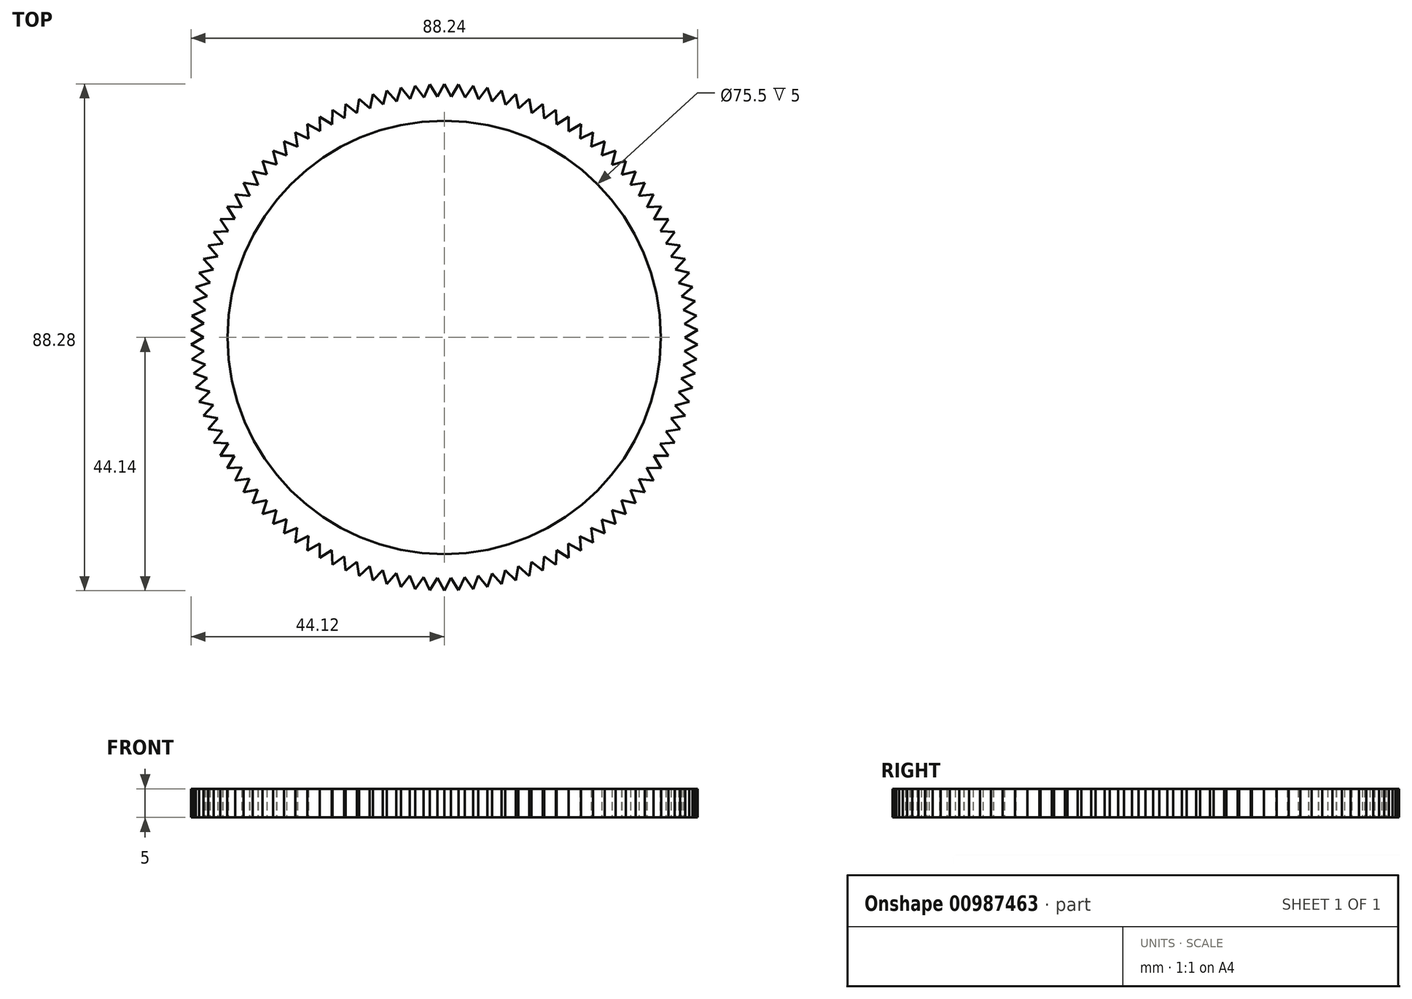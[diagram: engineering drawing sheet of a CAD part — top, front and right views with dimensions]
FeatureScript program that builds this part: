
annotation { "Feature Type Name" : "Feature", "Feature Type Description" : "" }
export const myFeature = defineFeature(function(context is Context, id is Id, definition is map)
    precondition{}
    {
        {
            var Q0;
            Q0=qCreatedBy(makeId("Top.planeOp"),FACE);
            var sketch = newSketch(context, id + "F0", { "sketchPlane" : qUnion([Q0])});
            skCircle(sketch, "E0", {"center": v(0, 0) * mm, "radius": 37.75 * mm});
            skCircle(sketch, "E1", {"center": v(0, 0) * mm, "radius": 41.84 * mm});
            skLineSegment(sketch, "E2", {"start": v(-1.23, 41.82) * mm, "end": v(0, 44.14) * mm});
            skLineSegment(sketch, "E3", {"start": v(0, 44.14) * mm, "end": v(1.27, 41.82) * mm});
            skLineSegment(sketch, "E4.1.0", {"start": v(-3.61, 41.69) * mm, "end": v(-2.52, 44.07) * mm});
            skLineSegment(sketch, "E4.1.1", {"start": v(-2.52, 44.07) * mm, "end": v(-1.12, 41.83) * mm});
            skLineSegment(sketch, "E4.2.0", {"start": v(-5.99, 41.41) * mm, "end": v(-5.03, 43.85) * mm});
            skLineSegment(sketch, "E4.2.1", {"start": v(-5.03, 43.85) * mm, "end": v(-3.5, 41.7) * mm});
            skLineSegment(sketch, "E4.3.0", {"start": v(-8.34, 41) * mm, "end": v(-7.53, 43.5) * mm});
            skLineSegment(sketch, "E4.3.1", {"start": v(-7.53, 43.5) * mm, "end": v(-5.88, 41.43) * mm});
            skLineSegment(sketch, "E4.4.0", {"start": v(-10.67, 40.46) * mm, "end": v(-10, 43) * mm});
            skLineSegment(sketch, "E4.4.1", {"start": v(-10, 43) * mm, "end": v(-8.23, 41.02) * mm});
            skLineSegment(sketch, "E4.5.0", {"start": v(-12.96, 39.78) * mm, "end": v(-12.44, 42.35) * mm});
            skLineSegment(sketch, "E4.5.1", {"start": v(-12.44, 42.35) * mm, "end": v(-10.56, 40.49) * mm});
            skLineSegment(sketch, "E4.6.0", {"start": v(-15.21, 38.98) * mm, "end": v(-14.83, 41.57) * mm});
            skLineSegment(sketch, "E4.6.1", {"start": v(-14.83, 41.57) * mm, "end": v(-12.86, 39.82) * mm});
            skLineSegment(sketch, "E4.7.0", {"start": v(-17.41, 38.05) * mm, "end": v(-17.18, 40.66) * mm});
            skLineSegment(sketch, "E4.7.1", {"start": v(-17.18, 40.66) * mm, "end": v(-15.1, 39.02) * mm});
            skLineSegment(sketch, "E4.8.0", {"start": v(-19.55, 37) * mm, "end": v(-19.48, 39.61) * mm});
            skLineSegment(sketch, "E4.8.1", {"start": v(-19.48, 39.61) * mm, "end": v(-17.31, 38.1) * mm});
            skLineSegment(sketch, "E4.9.0", {"start": v(-21.63, 35.81) * mm, "end": v(-21.7, 38.44) * mm});
            skLineSegment(sketch, "E4.9.1", {"start": v(-21.7, 38.44) * mm, "end": v(-19.46, 37.04) * mm});
            skLineSegment(sketch, "E4.10.0", {"start": v(-23.64, 34.52) * mm, "end": v(-23.86, 37.13) * mm});
            skLineSegment(sketch, "E4.10.1", {"start": v(-23.86, 37.13) * mm, "end": v(-21.54, 35.87) * mm});
            skLineSegment(sketch, "E4.11.0", {"start": v(-25.58, 33.11) * mm, "end": v(-25.95, 35.71) * mm});
            skLineSegment(sketch, "E4.11.1", {"start": v(-25.95, 35.71) * mm, "end": v(-23.55, 34.58) * mm});
            skLineSegment(sketch, "E4.12.0", {"start": v(-27.43, 31.6) * mm, "end": v(-27.94, 34.17) * mm});
            skLineSegment(sketch, "E4.12.1", {"start": v(-27.94, 34.17) * mm, "end": v(-25.49, 33.18) * mm});
            skLineSegment(sketch, "E4.13.0", {"start": v(-29.18, 29.98) * mm, "end": v(-29.85, 32.52) * mm});
            skLineSegment(sketch, "E4.13.1", {"start": v(-29.85, 32.52) * mm, "end": v(-27.34, 31.67) * mm});
            skLineSegment(sketch, "E4.14.0", {"start": v(-30.85, 28.27) * mm, "end": v(-31.65, 30.76) * mm});
            skLineSegment(sketch, "E4.14.1", {"start": v(-31.65, 30.76) * mm, "end": v(-29.1, 30.06) * mm});
            skLineSegment(sketch, "E4.15.0", {"start": v(-32.41, 26.46) * mm, "end": v(-33.36, 28.9) * mm});
            skLineSegment(sketch, "E4.15.1", {"start": v(-33.36, 28.9) * mm, "end": v(-30.77, 28.35) * mm});
            skLineSegment(sketch, "E4.16.0", {"start": v(-33.87, 24.57) * mm, "end": v(-34.95, 26.95) * mm});
            skLineSegment(sketch, "E4.16.1", {"start": v(-34.95, 26.95) * mm, "end": v(-32.34, 26.55) * mm});
            skLineSegment(sketch, "E4.17.0", {"start": v(-35.22, 22.6) * mm, "end": v(-36.44, 24.91) * mm});
            skLineSegment(sketch, "E4.17.1", {"start": v(-36.44, 24.91) * mm, "end": v(-33.8, 24.66) * mm});
            skLineSegment(sketch, "E4.18.0", {"start": v(-36.45, 20.55) * mm, "end": v(-37.8, 22.8) * mm});
            skLineSegment(sketch, "E4.18.1", {"start": v(-37.8, 22.8) * mm, "end": v(-35.16, 22.69) * mm});
            skLineSegment(sketch, "E4.19.0", {"start": v(-37.56, 18.43) * mm, "end": v(-39.04, 20.6) * mm});
            skLineSegment(sketch, "E4.19.1", {"start": v(-39.04, 20.6) * mm, "end": v(-36.4, 20.64) * mm});
            skLineSegment(sketch, "E4.20.0", {"start": v(-38.55, 16.26) * mm, "end": v(-40.15, 18.34) * mm});
            skLineSegment(sketch, "E4.20.1", {"start": v(-40.15, 18.34) * mm, "end": v(-37.51, 18.53) * mm});
            skLineSegment(sketch, "E4.21.0", {"start": v(-39.42, 14.03) * mm, "end": v(-41.13, 16.01) * mm});
            skLineSegment(sketch, "E4.21.1", {"start": v(-41.13, 16.01) * mm, "end": v(-38.51, 16.36) * mm});
            skLineSegment(sketch, "E4.22.0", {"start": v(-40.16, 11.76) * mm, "end": v(-41.98, 13.64) * mm});
            skLineSegment(sketch, "E4.22.1", {"start": v(-41.98, 13.64) * mm, "end": v(-39.38, 14.13) * mm});
            skLineSegment(sketch, "E4.23.0", {"start": v(-40.76, 9.45) * mm, "end": v(-42.7, 11.22) * mm});
            skLineSegment(sketch, "E4.23.1", {"start": v(-42.7, 11.22) * mm, "end": v(-40.13, 11.86) * mm});
            skLineSegment(sketch, "E4.24.0", {"start": v(-41.23, 7.1) * mm, "end": v(-43.26, 8.77) * mm});
            skLineSegment(sketch, "E4.24.1", {"start": v(-43.26, 8.77) * mm, "end": v(-40.74, 9.55) * mm});
            skLineSegment(sketch, "E4.25.0", {"start": v(-41.57, 4.74) * mm, "end": v(-43.7, 6.28) * mm});
            skLineSegment(sketch, "E4.25.1", {"start": v(-43.7, 6.28) * mm, "end": v(-41.22, 7.21) * mm});
            skLineSegment(sketch, "E4.26.0", {"start": v(-41.78, 2.36) * mm, "end": v(-43.98, 3.78) * mm});
            skLineSegment(sketch, "E4.26.1", {"start": v(-43.98, 3.78) * mm, "end": v(-41.56, 4.85) * mm});
            skLineSegment(sketch, "E4.27.0", {"start": v(-41.84, -0.03) * mm, "end": v(-44.12, 1.26) * mm});
            skLineSegment(sketch, "E4.27.1", {"start": v(-44.12, 1.26) * mm, "end": v(-41.77, 2.47) * mm});
            skLineSegment(sketch, "E4.28.0", {"start": v(-41.77, -2.42) * mm, "end": v(-44.12, -1.26) * mm});
            skLineSegment(sketch, "E4.28.1", {"start": v(-44.12, -1.26) * mm, "end": v(-41.84, 0.08) * mm});
            skLineSegment(sketch, "E4.29.0", {"start": v(-41.57, -4.8) * mm, "end": v(-43.98, -3.78) * mm});
            skLineSegment(sketch, "E4.29.1", {"start": v(-43.98, -3.78) * mm, "end": v(-41.78, -2.31) * mm});
            skLineSegment(sketch, "E4.30.0", {"start": v(-41.22, -7.17) * mm, "end": v(-43.7, -6.28) * mm});
            skLineSegment(sketch, "E4.30.1", {"start": v(-43.7, -6.28) * mm, "end": v(-41.58, -4.7) * mm});
            skLineSegment(sketch, "E4.31.0", {"start": v(-40.75, -9.5) * mm, "end": v(-43.26, -8.77) * mm});
            skLineSegment(sketch, "E4.31.1", {"start": v(-43.26, -8.77) * mm, "end": v(-41.24, -7.06) * mm});
            skLineSegment(sketch, "E4.32.0", {"start": v(-40.14, -11.82) * mm, "end": v(-42.7, -11.22) * mm});
            skLineSegment(sketch, "E4.32.1", {"start": v(-42.7, -11.22) * mm, "end": v(-40.77, -9.4) * mm});
            skLineSegment(sketch, "E4.33.0", {"start": v(-39.4, -14.1) * mm, "end": v(-41.98, -13.64) * mm});
            skLineSegment(sketch, "E4.33.1", {"start": v(-41.98, -13.64) * mm, "end": v(-40.17, -11.71) * mm});
            skLineSegment(sketch, "E4.34.0", {"start": v(-38.53, -16.32) * mm, "end": v(-41.13, -16.01) * mm});
            skLineSegment(sketch, "E4.34.1", {"start": v(-41.13, -16.01) * mm, "end": v(-39.43, -13.99) * mm});
            skLineSegment(sketch, "E4.35.0", {"start": v(-37.53, -18.5) * mm, "end": v(-40.15, -18.34) * mm});
            skLineSegment(sketch, "E4.35.1", {"start": v(-40.15, -18.34) * mm, "end": v(-38.57, -16.22) * mm});
            skLineSegment(sketch, "E4.36.0", {"start": v(-36.42, -20.6) * mm, "end": v(-39.04, -20.6) * mm});
            skLineSegment(sketch, "E4.36.1", {"start": v(-39.04, -20.6) * mm, "end": v(-37.58, -18.4) * mm});
            skLineSegment(sketch, "E4.37.0", {"start": v(-35.18, -22.65) * mm, "end": v(-37.8, -22.8) * mm});
            skLineSegment(sketch, "E4.37.1", {"start": v(-37.8, -22.8) * mm, "end": v(-36.47, -20.5) * mm});
            skLineSegment(sketch, "E4.38.0", {"start": v(-33.83, -24.62) * mm, "end": v(-36.44, -24.91) * mm});
            skLineSegment(sketch, "E4.38.1", {"start": v(-36.44, -24.91) * mm, "end": v(-35.24, -22.56) * mm});
            skLineSegment(sketch, "E4.39.0", {"start": v(-32.37, -26.51) * mm, "end": v(-34.95, -26.95) * mm});
            skLineSegment(sketch, "E4.39.1", {"start": v(-34.95, -26.95) * mm, "end": v(-33.9, -24.53) * mm});
            skLineSegment(sketch, "E4.40.0", {"start": v(-30.8, -28.32) * mm, "end": v(-33.36, -28.9) * mm});
            skLineSegment(sketch, "E4.40.1", {"start": v(-33.36, -28.9) * mm, "end": v(-32.44, -26.43) * mm});
            skLineSegment(sketch, "E4.41.0", {"start": v(-29.14, -30.03) * mm, "end": v(-31.65, -30.76) * mm});
            skLineSegment(sketch, "E4.41.1", {"start": v(-31.65, -30.76) * mm, "end": v(-30.88, -28.24) * mm});
            skLineSegment(sketch, "E4.42.0", {"start": v(-27.38, -31.64) * mm, "end": v(-29.85, -32.52) * mm});
            skLineSegment(sketch, "E4.42.1", {"start": v(-29.85, -32.52) * mm, "end": v(-29.22, -29.95) * mm});
            skLineSegment(sketch, "E4.43.0", {"start": v(-25.52, -33.15) * mm, "end": v(-27.94, -34.17) * mm});
            skLineSegment(sketch, "E4.43.1", {"start": v(-27.94, -34.17) * mm, "end": v(-27.46, -31.57) * mm});
            skLineSegment(sketch, "E4.44.0", {"start": v(-23.6, -34.56) * mm, "end": v(-25.95, -35.71) * mm});
            skLineSegment(sketch, "E4.44.1", {"start": v(-25.95, -35.71) * mm, "end": v(-25.61, -33.09) * mm});
            skLineSegment(sketch, "E4.45.0", {"start": v(-21.58, -35.85) * mm, "end": v(-23.86, -37.13) * mm});
            skLineSegment(sketch, "E4.45.1", {"start": v(-23.86, -37.13) * mm, "end": v(-23.68, -34.5) * mm});
            skLineSegment(sketch, "E4.46.0", {"start": v(-19.5, -37.02) * mm, "end": v(-21.7, -38.44) * mm});
            skLineSegment(sketch, "E4.46.1", {"start": v(-21.7, -38.44) * mm, "end": v(-21.67, -35.8) * mm});
            skLineSegment(sketch, "E4.47.0", {"start": v(-17.35, -38.07) * mm, "end": v(-19.48, -39.61) * mm});
            skLineSegment(sketch, "E4.47.1", {"start": v(-19.48, -39.61) * mm, "end": v(-19.6, -36.97) * mm});
            skLineSegment(sketch, "E4.48.0", {"start": v(-15.15, -39) * mm, "end": v(-17.18, -40.66) * mm});
            skLineSegment(sketch, "E4.48.1", {"start": v(-17.18, -40.66) * mm, "end": v(-17.45, -38.03) * mm});
            skLineSegment(sketch, "E4.49.0", {"start": v(-12.9, -39.8) * mm, "end": v(-14.83, -41.57) * mm});
            skLineSegment(sketch, "E4.49.1", {"start": v(-14.83, -41.57) * mm, "end": v(-15.25, -38.96) * mm});
            skLineSegment(sketch, "E4.50.0", {"start": v(-10.6, -40.48) * mm, "end": v(-12.44, -42.35) * mm});
            skLineSegment(sketch, "E4.50.1", {"start": v(-12.44, -42.35) * mm, "end": v(-13, -39.77) * mm});
            skLineSegment(sketch, "E4.51.0", {"start": v(-8.28, -41.01) * mm, "end": v(-10, -43) * mm});
            skLineSegment(sketch, "E4.51.1", {"start": v(-10, -43) * mm, "end": v(-10.71, -40.45) * mm});
            skLineSegment(sketch, "E4.52.0", {"start": v(-5.92, -41.42) * mm, "end": v(-7.53, -43.5) * mm});
            skLineSegment(sketch, "E4.52.1", {"start": v(-7.53, -43.5) * mm, "end": v(-8.39, -41) * mm});
            skLineSegment(sketch, "E4.53.0", {"start": v(-3.55, -41.7) * mm, "end": v(-5.03, -43.85) * mm});
            skLineSegment(sketch, "E4.53.1", {"start": v(-5.03, -43.85) * mm, "end": v(-6.03, -41.4) * mm});
            skLineSegment(sketch, "E4.54.0", {"start": v(-1.16, -41.83) * mm, "end": v(-2.52, -44.07) * mm});
            skLineSegment(sketch, "E4.54.1", {"start": v(-2.52, -44.07) * mm, "end": v(-3.66, -41.68) * mm});
            skLineSegment(sketch, "E4.55.0", {"start": v(1.23, -41.82) * mm, "end": v(0, -44.14) * mm});
            skLineSegment(sketch, "E4.55.1", {"start": v(0, -44.14) * mm, "end": v(-1.27, -41.82) * mm});
            skLineSegment(sketch, "E4.56.0", {"start": v(3.61, -41.69) * mm, "end": v(2.52, -44.07) * mm});
            skLineSegment(sketch, "E4.56.1", {"start": v(2.52, -44.07) * mm, "end": v(1.12, -41.83) * mm});
            skLineSegment(sketch, "E4.57.0", {"start": v(5.99, -41.41) * mm, "end": v(5.03, -43.85) * mm});
            skLineSegment(sketch, "E4.57.1", {"start": v(5.03, -43.85) * mm, "end": v(3.5, -41.7) * mm});
            skLineSegment(sketch, "E4.58.0", {"start": v(8.34, -41) * mm, "end": v(7.53, -43.5) * mm});
            skLineSegment(sketch, "E4.58.1", {"start": v(7.53, -43.5) * mm, "end": v(5.88, -41.43) * mm});
            skLineSegment(sketch, "E4.59.0", {"start": v(10.67, -40.46) * mm, "end": v(10, -43) * mm});
            skLineSegment(sketch, "E4.59.1", {"start": v(10, -43) * mm, "end": v(8.23, -41.02) * mm});
            skLineSegment(sketch, "E4.60.0", {"start": v(12.96, -39.78) * mm, "end": v(12.44, -42.35) * mm});
            skLineSegment(sketch, "E4.60.1", {"start": v(12.44, -42.35) * mm, "end": v(10.56, -40.49) * mm});
            skLineSegment(sketch, "E4.61.0", {"start": v(15.21, -38.98) * mm, "end": v(14.83, -41.57) * mm});
            skLineSegment(sketch, "E4.61.1", {"start": v(14.83, -41.57) * mm, "end": v(12.86, -39.82) * mm});
            skLineSegment(sketch, "E4.62.0", {"start": v(17.41, -38.05) * mm, "end": v(17.18, -40.66) * mm});
            skLineSegment(sketch, "E4.62.1", {"start": v(17.18, -40.66) * mm, "end": v(15.1, -39.02) * mm});
            skLineSegment(sketch, "E4.63.0", {"start": v(19.55, -37) * mm, "end": v(19.48, -39.61) * mm});
            skLineSegment(sketch, "E4.63.1", {"start": v(19.48, -39.61) * mm, "end": v(17.31, -38.1) * mm});
            skLineSegment(sketch, "E4.64.0", {"start": v(21.63, -35.81) * mm, "end": v(21.7, -38.44) * mm});
            skLineSegment(sketch, "E4.64.1", {"start": v(21.7, -38.44) * mm, "end": v(19.46, -37.04) * mm});
            skLineSegment(sketch, "E4.65.0", {"start": v(23.64, -34.52) * mm, "end": v(23.86, -37.13) * mm});
            skLineSegment(sketch, "E4.65.1", {"start": v(23.86, -37.13) * mm, "end": v(21.54, -35.87) * mm});
            skLineSegment(sketch, "E4.66.0", {"start": v(25.58, -33.11) * mm, "end": v(25.95, -35.71) * mm});
            skLineSegment(sketch, "E4.66.1", {"start": v(25.95, -35.71) * mm, "end": v(23.55, -34.58) * mm});
            skLineSegment(sketch, "E4.67.0", {"start": v(27.43, -31.6) * mm, "end": v(27.94, -34.17) * mm});
            skLineSegment(sketch, "E4.67.1", {"start": v(27.94, -34.17) * mm, "end": v(25.49, -33.18) * mm});
            skLineSegment(sketch, "E4.68.0", {"start": v(29.18, -29.98) * mm, "end": v(29.85, -32.52) * mm});
            skLineSegment(sketch, "E4.68.1", {"start": v(29.85, -32.52) * mm, "end": v(27.34, -31.67) * mm});
            skLineSegment(sketch, "E4.69.0", {"start": v(30.85, -28.27) * mm, "end": v(31.65, -30.76) * mm});
            skLineSegment(sketch, "E4.69.1", {"start": v(31.65, -30.76) * mm, "end": v(29.1, -30.06) * mm});
            skLineSegment(sketch, "E4.70.0", {"start": v(32.41, -26.46) * mm, "end": v(33.36, -28.9) * mm});
            skLineSegment(sketch, "E4.70.1", {"start": v(33.36, -28.9) * mm, "end": v(30.77, -28.35) * mm});
            skLineSegment(sketch, "E4.71.0", {"start": v(33.87, -24.57) * mm, "end": v(34.95, -26.95) * mm});
            skLineSegment(sketch, "E4.71.1", {"start": v(34.95, -26.95) * mm, "end": v(32.34, -26.55) * mm});
            skLineSegment(sketch, "E4.72.0", {"start": v(35.22, -22.6) * mm, "end": v(36.44, -24.91) * mm});
            skLineSegment(sketch, "E4.72.1", {"start": v(36.44, -24.91) * mm, "end": v(33.8, -24.66) * mm});
            skLineSegment(sketch, "E4.73.0", {"start": v(36.45, -20.55) * mm, "end": v(37.8, -22.8) * mm});
            skLineSegment(sketch, "E4.73.1", {"start": v(37.8, -22.8) * mm, "end": v(35.16, -22.69) * mm});
            skLineSegment(sketch, "E4.74.0", {"start": v(37.56, -18.43) * mm, "end": v(39.04, -20.6) * mm});
            skLineSegment(sketch, "E4.74.1", {"start": v(39.04, -20.6) * mm, "end": v(36.4, -20.64) * mm});
            skLineSegment(sketch, "E4.75.0", {"start": v(38.55, -16.26) * mm, "end": v(40.15, -18.34) * mm});
            skLineSegment(sketch, "E4.75.1", {"start": v(40.15, -18.34) * mm, "end": v(37.51, -18.53) * mm});
            skLineSegment(sketch, "E4.76.0", {"start": v(39.42, -14.03) * mm, "end": v(41.13, -16.01) * mm});
            skLineSegment(sketch, "E4.76.1", {"start": v(41.13, -16.01) * mm, "end": v(38.51, -16.36) * mm});
            skLineSegment(sketch, "E4.77.0", {"start": v(40.16, -11.76) * mm, "end": v(41.98, -13.64) * mm});
            skLineSegment(sketch, "E4.77.1", {"start": v(41.98, -13.64) * mm, "end": v(39.38, -14.13) * mm});
            skLineSegment(sketch, "E4.78.0", {"start": v(40.76, -9.45) * mm, "end": v(42.7, -11.22) * mm});
            skLineSegment(sketch, "E4.78.1", {"start": v(42.7, -11.22) * mm, "end": v(40.13, -11.86) * mm});
            skLineSegment(sketch, "E4.79.0", {"start": v(41.23, -7.1) * mm, "end": v(43.26, -8.77) * mm});
            skLineSegment(sketch, "E4.79.1", {"start": v(43.26, -8.77) * mm, "end": v(40.74, -9.55) * mm});
            skLineSegment(sketch, "E4.80.0", {"start": v(41.57, -4.74) * mm, "end": v(43.7, -6.28) * mm});
            skLineSegment(sketch, "E4.80.1", {"start": v(43.7, -6.28) * mm, "end": v(41.22, -7.21) * mm});
            skLineSegment(sketch, "E4.81.0", {"start": v(41.78, -2.36) * mm, "end": v(43.98, -3.78) * mm});
            skLineSegment(sketch, "E4.81.1", {"start": v(43.98, -3.78) * mm, "end": v(41.56, -4.85) * mm});
            skLineSegment(sketch, "E4.82.0", {"start": v(41.84, 0.03) * mm, "end": v(44.12, -1.26) * mm});
            skLineSegment(sketch, "E4.82.1", {"start": v(44.12, -1.26) * mm, "end": v(41.77, -2.47) * mm});
            skLineSegment(sketch, "E4.83.0", {"start": v(41.77, 2.42) * mm, "end": v(44.12, 1.26) * mm});
            skLineSegment(sketch, "E4.83.1", {"start": v(44.12, 1.26) * mm, "end": v(41.84, -0.08) * mm});
            skLineSegment(sketch, "E4.84.0", {"start": v(41.57, 4.8) * mm, "end": v(43.98, 3.78) * mm});
            skLineSegment(sketch, "E4.84.1", {"start": v(43.98, 3.78) * mm, "end": v(41.78, 2.31) * mm});
            skLineSegment(sketch, "E4.85.0", {"start": v(41.22, 7.17) * mm, "end": v(43.7, 6.28) * mm});
            skLineSegment(sketch, "E4.85.1", {"start": v(43.7, 6.28) * mm, "end": v(41.58, 4.7) * mm});
            skLineSegment(sketch, "E4.86.0", {"start": v(40.75, 9.5) * mm, "end": v(43.26, 8.77) * mm});
            skLineSegment(sketch, "E4.86.1", {"start": v(43.26, 8.77) * mm, "end": v(41.24, 7.06) * mm});
            skLineSegment(sketch, "E4.87.0", {"start": v(40.14, 11.82) * mm, "end": v(42.7, 11.22) * mm});
            skLineSegment(sketch, "E4.87.1", {"start": v(42.7, 11.22) * mm, "end": v(40.77, 9.4) * mm});
            skLineSegment(sketch, "E4.88.0", {"start": v(39.4, 14.1) * mm, "end": v(41.98, 13.64) * mm});
            skLineSegment(sketch, "E4.88.1", {"start": v(41.98, 13.64) * mm, "end": v(40.17, 11.71) * mm});
            skLineSegment(sketch, "E4.89.0", {"start": v(38.53, 16.32) * mm, "end": v(41.13, 16.01) * mm});
            skLineSegment(sketch, "E4.89.1", {"start": v(41.13, 16.01) * mm, "end": v(39.43, 13.99) * mm});
            skLineSegment(sketch, "E4.90.0", {"start": v(37.53, 18.5) * mm, "end": v(40.15, 18.34) * mm});
            skLineSegment(sketch, "E4.90.1", {"start": v(40.15, 18.34) * mm, "end": v(38.57, 16.22) * mm});
            skLineSegment(sketch, "E4.91.0", {"start": v(36.42, 20.6) * mm, "end": v(39.04, 20.6) * mm});
            skLineSegment(sketch, "E4.91.1", {"start": v(39.04, 20.6) * mm, "end": v(37.58, 18.4) * mm});
            skLineSegment(sketch, "E4.92.0", {"start": v(35.18, 22.65) * mm, "end": v(37.8, 22.8) * mm});
            skLineSegment(sketch, "E4.92.1", {"start": v(37.8, 22.8) * mm, "end": v(36.47, 20.5) * mm});
            skLineSegment(sketch, "E4.93.0", {"start": v(33.83, 24.62) * mm, "end": v(36.44, 24.91) * mm});
            skLineSegment(sketch, "E4.93.1", {"start": v(36.44, 24.91) * mm, "end": v(35.24, 22.56) * mm});
            skLineSegment(sketch, "E4.94.0", {"start": v(32.37, 26.51) * mm, "end": v(34.95, 26.95) * mm});
            skLineSegment(sketch, "E4.94.1", {"start": v(34.95, 26.95) * mm, "end": v(33.9, 24.53) * mm});
            skLineSegment(sketch, "E4.95.0", {"start": v(30.8, 28.32) * mm, "end": v(33.36, 28.9) * mm});
            skLineSegment(sketch, "E4.95.1", {"start": v(33.36, 28.9) * mm, "end": v(32.44, 26.43) * mm});
            skLineSegment(sketch, "E4.96.0", {"start": v(29.14, 30.03) * mm, "end": v(31.65, 30.76) * mm});
            skLineSegment(sketch, "E4.96.1", {"start": v(31.65, 30.76) * mm, "end": v(30.88, 28.24) * mm});
            skLineSegment(sketch, "E4.97.0", {"start": v(27.38, 31.64) * mm, "end": v(29.85, 32.52) * mm});
            skLineSegment(sketch, "E4.97.1", {"start": v(29.85, 32.52) * mm, "end": v(29.22, 29.95) * mm});
            skLineSegment(sketch, "E4.98.0", {"start": v(25.52, 33.15) * mm, "end": v(27.94, 34.17) * mm});
            skLineSegment(sketch, "E4.98.1", {"start": v(27.94, 34.17) * mm, "end": v(27.46, 31.57) * mm});
            skLineSegment(sketch, "E4.99.0", {"start": v(23.6, 34.56) * mm, "end": v(25.95, 35.71) * mm});
            skLineSegment(sketch, "E4.99.1", {"start": v(25.95, 35.71) * mm, "end": v(25.61, 33.09) * mm});
            skLineSegment(sketch, "E4.100.0", {"start": v(21.58, 35.85) * mm, "end": v(23.86, 37.13) * mm});
            skLineSegment(sketch, "E4.100.1", {"start": v(23.86, 37.13) * mm, "end": v(23.68, 34.5) * mm});
            skLineSegment(sketch, "E4.101.0", {"start": v(19.5, 37.02) * mm, "end": v(21.7, 38.44) * mm});
            skLineSegment(sketch, "E4.101.1", {"start": v(21.7, 38.44) * mm, "end": v(21.67, 35.8) * mm});
            skLineSegment(sketch, "E4.102.0", {"start": v(17.35, 38.07) * mm, "end": v(19.48, 39.61) * mm});
            skLineSegment(sketch, "E4.102.1", {"start": v(19.48, 39.61) * mm, "end": v(19.6, 36.97) * mm});
            skLineSegment(sketch, "E4.103.0", {"start": v(15.15, 39) * mm, "end": v(17.18, 40.66) * mm});
            skLineSegment(sketch, "E4.103.1", {"start": v(17.18, 40.66) * mm, "end": v(17.45, 38.03) * mm});
            skLineSegment(sketch, "E4.104.0", {"start": v(12.9, 39.8) * mm, "end": v(14.83, 41.57) * mm});
            skLineSegment(sketch, "E4.104.1", {"start": v(14.83, 41.57) * mm, "end": v(15.25, 38.96) * mm});
            skLineSegment(sketch, "E4.105.0", {"start": v(10.6, 40.48) * mm, "end": v(12.44, 42.35) * mm});
            skLineSegment(sketch, "E4.105.1", {"start": v(12.44, 42.35) * mm, "end": v(13, 39.77) * mm});
            skLineSegment(sketch, "E4.106.0", {"start": v(8.28, 41.01) * mm, "end": v(10, 43) * mm});
            skLineSegment(sketch, "E4.106.1", {"start": v(10, 43) * mm, "end": v(10.71, 40.45) * mm});
            skLineSegment(sketch, "E4.107.0", {"start": v(5.92, 41.42) * mm, "end": v(7.53, 43.5) * mm});
            skLineSegment(sketch, "E4.107.1", {"start": v(7.53, 43.5) * mm, "end": v(8.39, 41) * mm});
            skLineSegment(sketch, "E4.108.0", {"start": v(3.55, 41.7) * mm, "end": v(5.03, 43.85) * mm});
            skLineSegment(sketch, "E4.108.1", {"start": v(5.03, 43.85) * mm, "end": v(6.03, 41.4) * mm});
            skLineSegment(sketch, "E4.109.0", {"start": v(1.16, 41.83) * mm, "end": v(2.52, 44.07) * mm});
            skLineSegment(sketch, "E4.109.1", {"start": v(2.52, 44.07) * mm, "end": v(3.66, 41.68) * mm});
            skSolve(sketch);
        }
        {
            var Q0;
            Q0=makeQuery(id+"F0.imprint","IMPRINT",FACE,{"disambiguationData":[TD([[makeQuery(id+"F0.imprint","IMPRINT",EDGE,{"derivedFrom":sQuery(id+"F0.wireOp",EDGE,"E0")}),-1.0]])]});
            var Q1;
            {var subQ3=sQuery(id+"F0.wireOp",EDGE,"E4.88.0");var subQ7=sQuery(id+"F0.wireOp",EDGE,"E1");var subQ8=makeQuery(id+"F0.imprint","INTERSECT",VERTEX,{"derivedFrom":[subQ7,subQ3]});Q1=makeQuery(id+"F0.imprint","IMPRINT",FACE,{"disambiguationData":[TD([[makeQuery(id+"F0.imprint","IMPRINT",EDGE,{"disambiguationData":[TD([[subQ8,-1.0]])],"derivedFrom":subQ7}),-1.0]])]});}
            var Q2;
            {var subQ5=sQuery(id+"F0.wireOp",EDGE,"E4.100.0");var subQ6=sQuery(id+"F0.wireOp",EDGE,"E1");var subQ7=makeQuery(id+"F0.imprint","INTERSECT",VERTEX,{"derivedFrom":[subQ6,subQ5]});Q2=makeQuery(id+"F0.imprint","IMPRINT",FACE,{"disambiguationData":[TD([[makeQuery(id+"F0.imprint","IMPRINT",EDGE,{"disambiguationData":[TD([[subQ7,-1.0]])],"derivedFrom":subQ6}),-1.0]])]});}
            var Q3;
            {var subQ5=sQuery(id+"F0.wireOp",EDGE,"E4.20.0");var subQ6=sQuery(id+"F0.wireOp",EDGE,"E1");var subQ7=makeQuery(id+"F0.imprint","INTERSECT",VERTEX,{"derivedFrom":[subQ6,subQ5]});Q3=makeQuery(id+"F0.imprint","IMPRINT",FACE,{"disambiguationData":[TD([[makeQuery(id+"F0.imprint","IMPRINT",EDGE,{"disambiguationData":[TD([[subQ7,-1.0]])],"derivedFrom":subQ6}),-1.0]])]});}
            var Q4;
            {var subQ5=sQuery(id+"F0.wireOp",EDGE,"E4.25.0");var subQ6=sQuery(id+"F0.wireOp",EDGE,"E1");var subQ7=makeQuery(id+"F0.imprint","INTERSECT",VERTEX,{"derivedFrom":[subQ6,subQ5]});Q4=makeQuery(id+"F0.imprint","IMPRINT",FACE,{"disambiguationData":[TD([[makeQuery(id+"F0.imprint","IMPRINT",EDGE,{"disambiguationData":[TD([[subQ7,-1.0]])],"derivedFrom":subQ6}),-1.0]])]});}
            var Q5;
            {var subQ3=sQuery(id+"F0.wireOp",EDGE,"E4.13.0");var subQ7=sQuery(id+"F0.wireOp",EDGE,"E1");var subQ8=makeQuery(id+"F0.imprint","INTERSECT",VERTEX,{"derivedFrom":[subQ7,subQ3]});Q5=makeQuery(id+"F0.imprint","IMPRINT",FACE,{"disambiguationData":[TD([[makeQuery(id+"F0.imprint","IMPRINT",EDGE,{"disambiguationData":[TD([[subQ8,-1.0]])],"derivedFrom":subQ7}),-1.0]])]});}
            var Q6;
            {var subQ3=sQuery(id+"F0.wireOp",EDGE,"E4.12.0");var subQ7=sQuery(id+"F0.wireOp",EDGE,"E1");var subQ8=makeQuery(id+"F0.imprint","INTERSECT",VERTEX,{"derivedFrom":[subQ7,subQ3]});Q6=makeQuery(id+"F0.imprint","IMPRINT",FACE,{"disambiguationData":[TD([[makeQuery(id+"F0.imprint","IMPRINT",EDGE,{"disambiguationData":[TD([[subQ8,-1.0]])],"derivedFrom":subQ7}),-1.0]])]});}
            var Q7;
            {var subQ3=sQuery(id+"F0.wireOp",EDGE,"E4.79.0");var subQ7=sQuery(id+"F0.wireOp",EDGE,"E1");var subQ8=makeQuery(id+"F0.imprint","INTERSECT",VERTEX,{"derivedFrom":[subQ7,subQ3]});Q7=makeQuery(id+"F0.imprint","IMPRINT",FACE,{"disambiguationData":[TD([[makeQuery(id+"F0.imprint","IMPRINT",EDGE,{"disambiguationData":[TD([[subQ8,-1.0]])],"derivedFrom":subQ7}),-1.0]])]});}
            var Q8;
            {var subQ5=sQuery(id+"F0.wireOp",EDGE,"E4.75.0");var subQ6=sQuery(id+"F0.wireOp",EDGE,"E1");var subQ7=makeQuery(id+"F0.imprint","INTERSECT",VERTEX,{"derivedFrom":[subQ6,subQ5]});Q8=makeQuery(id+"F0.imprint","IMPRINT",FACE,{"disambiguationData":[TD([[makeQuery(id+"F0.imprint","IMPRINT",EDGE,{"disambiguationData":[TD([[subQ7,-1.0]])],"derivedFrom":subQ6}),-1.0]])]});}
            var Q9;
            {var subQ3=sQuery(id+"F0.wireOp",EDGE,"E4.34.0");var subQ7=sQuery(id+"F0.wireOp",EDGE,"E1");var subQ8=makeQuery(id+"F0.imprint","INTERSECT",VERTEX,{"derivedFrom":[subQ7,subQ3]});Q9=makeQuery(id+"F0.imprint","IMPRINT",FACE,{"disambiguationData":[TD([[makeQuery(id+"F0.imprint","IMPRINT",EDGE,{"disambiguationData":[TD([[subQ8,-1.0]])],"derivedFrom":subQ7}),-1.0]])]});}
            var Q10;
            {var subQ3=sQuery(id+"F0.wireOp",EDGE,"E4.42.0");var subQ7=sQuery(id+"F0.wireOp",EDGE,"E1");var subQ8=makeQuery(id+"F0.imprint","INTERSECT",VERTEX,{"derivedFrom":[subQ7,subQ3]});Q10=makeQuery(id+"F0.imprint","IMPRINT",FACE,{"disambiguationData":[TD([[makeQuery(id+"F0.imprint","IMPRINT",EDGE,{"disambiguationData":[TD([[subQ8,-1.0]])],"derivedFrom":subQ7}),-1.0]])]});}
            var Q11;
            {var subQ3=sQuery(id+"F0.wireOp",EDGE,"E4.41.0");var subQ7=sQuery(id+"F0.wireOp",EDGE,"E1");var subQ8=makeQuery(id+"F0.imprint","INTERSECT",VERTEX,{"derivedFrom":[subQ7,subQ3]});Q11=makeQuery(id+"F0.imprint","IMPRINT",FACE,{"disambiguationData":[TD([[makeQuery(id+"F0.imprint","IMPRINT",EDGE,{"disambiguationData":[TD([[subQ8,-1.0]])],"derivedFrom":subQ7}),-1.0]])]});}
            var Q12;
            {var subQ5=sQuery(id+"F0.wireOp",EDGE,"E4.45.0");var subQ6=sQuery(id+"F0.wireOp",EDGE,"E1");var subQ7=makeQuery(id+"F0.imprint","INTERSECT",VERTEX,{"derivedFrom":[subQ6,subQ5]});Q12=makeQuery(id+"F0.imprint","IMPRINT",FACE,{"disambiguationData":[TD([[makeQuery(id+"F0.imprint","IMPRINT",EDGE,{"disambiguationData":[TD([[subQ7,-1.0]])],"derivedFrom":subQ6}),-1.0]])]});}
            var Q13;
            {var subQ3=sQuery(id+"F0.wireOp",EDGE,"E4.59.0");var subQ7=sQuery(id+"F0.wireOp",EDGE,"E1");var subQ8=makeQuery(id+"F0.imprint","INTERSECT",VERTEX,{"derivedFrom":[subQ7,subQ3]});Q13=makeQuery(id+"F0.imprint","IMPRINT",FACE,{"disambiguationData":[TD([[makeQuery(id+"F0.imprint","IMPRINT",EDGE,{"disambiguationData":[TD([[subQ8,-1.0]])],"derivedFrom":subQ7}),-1.0]])]});}
            var Q14;
            {var subQ3=sQuery(id+"F0.wireOp",EDGE,"E4.76.0");var subQ7=sQuery(id+"F0.wireOp",EDGE,"E1");var subQ8=makeQuery(id+"F0.imprint","INTERSECT",VERTEX,{"derivedFrom":[subQ7,subQ3]});Q14=makeQuery(id+"F0.imprint","IMPRINT",FACE,{"disambiguationData":[TD([[makeQuery(id+"F0.imprint","IMPRINT",EDGE,{"disambiguationData":[TD([[subQ8,-1.0]])],"derivedFrom":subQ7}),-1.0]])]});}
            var Q15;
            {var subQ3=sQuery(id+"F0.wireOp",EDGE,"E4.73.0");var subQ7=sQuery(id+"F0.wireOp",EDGE,"E1");var subQ8=makeQuery(id+"F0.imprint","INTERSECT",VERTEX,{"derivedFrom":[subQ7,subQ3]});Q15=makeQuery(id+"F0.imprint","IMPRINT",FACE,{"disambiguationData":[TD([[makeQuery(id+"F0.imprint","IMPRINT",EDGE,{"disambiguationData":[TD([[subQ8,-1.0]])],"derivedFrom":subQ7}),-1.0]])]});}
            var Q16;
            {var subQ5=sQuery(id+"F0.wireOp",EDGE,"E4.70.0");var subQ6=sQuery(id+"F0.wireOp",EDGE,"E1");var subQ7=makeQuery(id+"F0.imprint","INTERSECT",VERTEX,{"derivedFrom":[subQ6,subQ5]});Q16=makeQuery(id+"F0.imprint","IMPRINT",FACE,{"disambiguationData":[TD([[makeQuery(id+"F0.imprint","IMPRINT",EDGE,{"disambiguationData":[TD([[subQ7,-1.0]])],"derivedFrom":subQ6}),-1.0]])]});}
            var Q17;
            {var subQ3=sQuery(id+"F0.wireOp",EDGE,"E4.69.0");var subQ5=sQuery(id+"F0.wireOp",EDGE,"E1");var subQ6=makeQuery(id+"F0.imprint","INTERSECT",VERTEX,{"derivedFrom":[subQ5,subQ3]});Q17=makeQuery(id+"F0.imprint","IMPRINT",FACE,{"disambiguationData":[TD([[makeQuery(id+"F0.imprint","IMPRINT",EDGE,{"disambiguationData":[TD([[subQ6,-1.0]])],"derivedFrom":subQ5}),-1.0]])]});}
            var Q18;
            {var subQ3=sQuery(id+"F0.wireOp",EDGE,"E4.68.0");var subQ7=sQuery(id+"F0.wireOp",EDGE,"E1");var subQ8=makeQuery(id+"F0.imprint","INTERSECT",VERTEX,{"derivedFrom":[subQ7,subQ3]});Q18=makeQuery(id+"F0.imprint","IMPRINT",FACE,{"disambiguationData":[TD([[makeQuery(id+"F0.imprint","IMPRINT",EDGE,{"disambiguationData":[TD([[subQ8,-1.0]])],"derivedFrom":subQ7}),-1.0]])]});}
            var Q19;
            {var subQ3=sQuery(id+"F0.wireOp",EDGE,"E4.67.0");var subQ7=sQuery(id+"F0.wireOp",EDGE,"E1");var subQ8=makeQuery(id+"F0.imprint","INTERSECT",VERTEX,{"derivedFrom":[subQ7,subQ3]});Q19=makeQuery(id+"F0.imprint","IMPRINT",FACE,{"disambiguationData":[TD([[makeQuery(id+"F0.imprint","IMPRINT",EDGE,{"disambiguationData":[TD([[subQ8,-1.0]])],"derivedFrom":subQ7}),-1.0]])]});}
            var Q20;
            {var subQ3=sQuery(id+"F0.wireOp",EDGE,"E4.66.0");var subQ7=sQuery(id+"F0.wireOp",EDGE,"E1");var subQ8=makeQuery(id+"F0.imprint","INTERSECT",VERTEX,{"derivedFrom":[subQ7,subQ3]});Q20=makeQuery(id+"F0.imprint","IMPRINT",FACE,{"disambiguationData":[TD([[makeQuery(id+"F0.imprint","IMPRINT",EDGE,{"disambiguationData":[TD([[subQ8,-1.0]])],"derivedFrom":subQ7}),-1.0]])]});}
            var Q21;
            {var subQ5=sQuery(id+"F0.wireOp",EDGE,"E4.65.0");var subQ6=sQuery(id+"F0.wireOp",EDGE,"E1");var subQ7=makeQuery(id+"F0.imprint","INTERSECT",VERTEX,{"derivedFrom":[subQ6,subQ5]});Q21=makeQuery(id+"F0.imprint","IMPRINT",FACE,{"disambiguationData":[TD([[makeQuery(id+"F0.imprint","IMPRINT",EDGE,{"disambiguationData":[TD([[subQ7,-1.0]])],"derivedFrom":subQ6}),-1.0]])]});}
            var Q22;
            {var subQ3=sQuery(id+"F0.wireOp",EDGE,"E4.64.0");var subQ7=sQuery(id+"F0.wireOp",EDGE,"E1");var subQ8=makeQuery(id+"F0.imprint","INTERSECT",VERTEX,{"derivedFrom":[subQ7,subQ3]});Q22=makeQuery(id+"F0.imprint","IMPRINT",FACE,{"disambiguationData":[TD([[makeQuery(id+"F0.imprint","IMPRINT",EDGE,{"disambiguationData":[TD([[subQ8,-1.0]])],"derivedFrom":subQ7}),-1.0]])]});}
            var Q23;
            {var subQ3=sQuery(id+"F0.wireOp",EDGE,"E4.63.0");var subQ7=sQuery(id+"F0.wireOp",EDGE,"E1");var subQ8=makeQuery(id+"F0.imprint","INTERSECT",VERTEX,{"derivedFrom":[subQ7,subQ3]});Q23=makeQuery(id+"F0.imprint","IMPRINT",FACE,{"disambiguationData":[TD([[makeQuery(id+"F0.imprint","IMPRINT",EDGE,{"disambiguationData":[TD([[subQ8,-1.0]])],"derivedFrom":subQ7}),-1.0]])]});}
            var Q24;
            {var subQ3=sQuery(id+"F0.wireOp",EDGE,"E4.62.0");var subQ7=sQuery(id+"F0.wireOp",EDGE,"E1");var subQ8=makeQuery(id+"F0.imprint","INTERSECT",VERTEX,{"derivedFrom":[subQ7,subQ3]});Q24=makeQuery(id+"F0.imprint","IMPRINT",FACE,{"disambiguationData":[TD([[makeQuery(id+"F0.imprint","IMPRINT",EDGE,{"disambiguationData":[TD([[subQ8,-1.0]])],"derivedFrom":subQ7}),-1.0]])]});}
            var Q25;
            {var subQ3=sQuery(id+"F0.wireOp",EDGE,"E4.61.0");var subQ7=sQuery(id+"F0.wireOp",EDGE,"E1");var subQ8=makeQuery(id+"F0.imprint","INTERSECT",VERTEX,{"derivedFrom":[subQ7,subQ3]});Q25=makeQuery(id+"F0.imprint","IMPRINT",FACE,{"disambiguationData":[TD([[makeQuery(id+"F0.imprint","IMPRINT",EDGE,{"disambiguationData":[TD([[subQ8,-1.0]])],"derivedFrom":subQ7}),-1.0]])]});}
            var Q26;
            {var subQ5=sQuery(id+"F0.wireOp",EDGE,"E4.90.0");var subQ6=sQuery(id+"F0.wireOp",EDGE,"E1");var subQ7=makeQuery(id+"F0.imprint","INTERSECT",VERTEX,{"derivedFrom":[subQ6,subQ5]});Q26=makeQuery(id+"F0.imprint","IMPRINT",FACE,{"disambiguationData":[TD([[makeQuery(id+"F0.imprint","IMPRINT",EDGE,{"disambiguationData":[TD([[subQ7,-1.0]])],"derivedFrom":subQ6}),-1.0]])]});}
            var Q27;
            {var subQ5=sQuery(id+"F0.wireOp",EDGE,"E4.80.0");var subQ6=sQuery(id+"F0.wireOp",EDGE,"E1");var subQ7=makeQuery(id+"F0.imprint","INTERSECT",VERTEX,{"derivedFrom":[subQ6,subQ5]});Q27=makeQuery(id+"F0.imprint","IMPRINT",FACE,{"disambiguationData":[TD([[makeQuery(id+"F0.imprint","IMPRINT",EDGE,{"disambiguationData":[TD([[subQ7,-1.0]])],"derivedFrom":subQ6}),-1.0]])]});}
            var Q28;
            {var subQ3=sQuery(id+"F0.wireOp",EDGE,"E4.91.0");var subQ5=sQuery(id+"F0.wireOp",EDGE,"E1");var subQ6=makeQuery(id+"F0.imprint","INTERSECT",VERTEX,{"derivedFrom":[subQ5,subQ3]});Q28=makeQuery(id+"F0.imprint","IMPRINT",FACE,{"disambiguationData":[TD([[makeQuery(id+"F0.imprint","IMPRINT",EDGE,{"disambiguationData":[TD([[subQ6,-1.0]])],"derivedFrom":subQ5}),-1.0]])]});}
            var Q29;
            {var subQ3=sQuery(id+"F0.wireOp",EDGE,"E4.81.0");var subQ7=sQuery(id+"F0.wireOp",EDGE,"E1");var subQ8=makeQuery(id+"F0.imprint","INTERSECT",VERTEX,{"derivedFrom":[subQ7,subQ3]});Q29=makeQuery(id+"F0.imprint","IMPRINT",FACE,{"disambiguationData":[TD([[makeQuery(id+"F0.imprint","IMPRINT",EDGE,{"disambiguationData":[TD([[subQ8,-1.0]])],"derivedFrom":subQ7}),-1.0]])]});}
            var Q30;
            {var subQ3=sQuery(id+"F0.wireOp",EDGE,"E4.92.0");var subQ7=sQuery(id+"F0.wireOp",EDGE,"E1");var subQ8=makeQuery(id+"F0.imprint","INTERSECT",VERTEX,{"derivedFrom":[subQ7,subQ3]});Q30=makeQuery(id+"F0.imprint","IMPRINT",FACE,{"disambiguationData":[TD([[makeQuery(id+"F0.imprint","IMPRINT",EDGE,{"disambiguationData":[TD([[subQ8,-1.0]])],"derivedFrom":subQ7}),-1.0]])]});}
            var Q31;
            {var subQ3=sQuery(id+"F0.wireOp",EDGE,"E4.93.0");var subQ7=sQuery(id+"F0.wireOp",EDGE,"E1");var subQ8=makeQuery(id+"F0.imprint","INTERSECT",VERTEX,{"derivedFrom":[subQ7,subQ3]});Q31=makeQuery(id+"F0.imprint","IMPRINT",FACE,{"disambiguationData":[TD([[makeQuery(id+"F0.imprint","IMPRINT",EDGE,{"disambiguationData":[TD([[subQ8,-1.0]])],"derivedFrom":subQ7}),-1.0]])]});}
            var Q32;
            {var subQ3=sQuery(id+"F0.wireOp",EDGE,"E4.94.0");var subQ7=sQuery(id+"F0.wireOp",EDGE,"E1");var subQ8=makeQuery(id+"F0.imprint","INTERSECT",VERTEX,{"derivedFrom":[subQ7,subQ3]});Q32=makeQuery(id+"F0.imprint","IMPRINT",FACE,{"disambiguationData":[TD([[makeQuery(id+"F0.imprint","IMPRINT",EDGE,{"disambiguationData":[TD([[subQ8,-1.0]])],"derivedFrom":subQ7}),-1.0]])]});}
            var Q33;
            {var subQ5=sQuery(id+"F0.wireOp",EDGE,"E4.95.0");var subQ6=sQuery(id+"F0.wireOp",EDGE,"E1");var subQ7=makeQuery(id+"F0.imprint","INTERSECT",VERTEX,{"derivedFrom":[subQ6,subQ5]});Q33=makeQuery(id+"F0.imprint","IMPRINT",FACE,{"disambiguationData":[TD([[makeQuery(id+"F0.imprint","IMPRINT",EDGE,{"disambiguationData":[TD([[subQ7,-1.0]])],"derivedFrom":subQ6}),-1.0]])]});}
            var Q34;
            {var subQ3=sQuery(id+"F0.wireOp",EDGE,"E4.96.0");var subQ7=sQuery(id+"F0.wireOp",EDGE,"E1");var subQ8=makeQuery(id+"F0.imprint","INTERSECT",VERTEX,{"derivedFrom":[subQ7,subQ3]});Q34=makeQuery(id+"F0.imprint","IMPRINT",FACE,{"disambiguationData":[TD([[makeQuery(id+"F0.imprint","IMPRINT",EDGE,{"disambiguationData":[TD([[subQ8,-1.0]])],"derivedFrom":subQ7}),-1.0]])]});}
            var Q35;
            {var subQ3=sQuery(id+"F0.wireOp",EDGE,"E4.97.0");var subQ7=sQuery(id+"F0.wireOp",EDGE,"E1");var subQ8=makeQuery(id+"F0.imprint","INTERSECT",VERTEX,{"derivedFrom":[subQ7,subQ3]});Q35=makeQuery(id+"F0.imprint","IMPRINT",FACE,{"disambiguationData":[TD([[makeQuery(id+"F0.imprint","IMPRINT",EDGE,{"disambiguationData":[TD([[subQ8,-1.0]])],"derivedFrom":subQ7}),-1.0]])]});}
            var Q36;
            {var subQ3=sQuery(id+"F0.wireOp",EDGE,"E4.98.0");var subQ7=sQuery(id+"F0.wireOp",EDGE,"E1");var subQ8=makeQuery(id+"F0.imprint","INTERSECT",VERTEX,{"derivedFrom":[subQ7,subQ3]});Q36=makeQuery(id+"F0.imprint","IMPRINT",FACE,{"disambiguationData":[TD([[makeQuery(id+"F0.imprint","IMPRINT",EDGE,{"disambiguationData":[TD([[subQ8,-1.0]])],"derivedFrom":subQ7}),-1.0]])]});}
            var Q37;
            {var subQ3=sQuery(id+"F0.wireOp",EDGE,"E4.99.0");var subQ7=sQuery(id+"F0.wireOp",EDGE,"E1");var subQ8=makeQuery(id+"F0.imprint","INTERSECT",VERTEX,{"derivedFrom":[subQ7,subQ3]});Q37=makeQuery(id+"F0.imprint","IMPRINT",FACE,{"disambiguationData":[TD([[makeQuery(id+"F0.imprint","IMPRINT",EDGE,{"disambiguationData":[TD([[subQ8,-1.0]])],"derivedFrom":subQ7}),-1.0]])]});}
            var Q38;
            {var subQ0=sQuery(id+"F0.wireOp",EDGE,"E4.100.0");var subQ1=sQuery(id+"F0.wireOp",EDGE,"E1");var subQ2=makeQuery(id+"F0.imprint","INTERSECT",VERTEX,{"derivedFrom":[subQ1,subQ0]});Q38=makeQuery(id+"F0.imprint","IMPRINT",FACE,{"disambiguationData":[TD([[makeQuery(id+"F0.imprint","IMPRINT",EDGE,{"disambiguationData":[TD([[subQ2,1.0]])],"derivedFrom":subQ1}),-1.0]])]});}
            var Q39;
            {var subQ3=sQuery(id+"F0.wireOp",EDGE,"E4.101.0");var subQ7=sQuery(id+"F0.wireOp",EDGE,"E1");var subQ8=makeQuery(id+"F0.imprint","INTERSECT",VERTEX,{"derivedFrom":[subQ7,subQ3]});Q39=makeQuery(id+"F0.imprint","IMPRINT",FACE,{"disambiguationData":[TD([[makeQuery(id+"F0.imprint","IMPRINT",EDGE,{"disambiguationData":[TD([[subQ8,-1.0]])],"derivedFrom":subQ7}),-1.0]])]});}
            var Q40;
            {var subQ3=sQuery(id+"F0.wireOp",EDGE,"E4.102.0");var subQ5=sQuery(id+"F0.wireOp",EDGE,"E1");var subQ6=makeQuery(id+"F0.imprint","INTERSECT",VERTEX,{"derivedFrom":[subQ5,subQ3]});Q40=makeQuery(id+"F0.imprint","IMPRINT",FACE,{"disambiguationData":[TD([[makeQuery(id+"F0.imprint","IMPRINT",EDGE,{"disambiguationData":[TD([[subQ6,-1.0]])],"derivedFrom":subQ5}),-1.0]])]});}
            var Q41;
            {var subQ3=sQuery(id+"F0.wireOp",EDGE,"E4.103.0");var subQ7=sQuery(id+"F0.wireOp",EDGE,"E1");var subQ8=makeQuery(id+"F0.imprint","INTERSECT",VERTEX,{"derivedFrom":[subQ7,subQ3]});Q41=makeQuery(id+"F0.imprint","IMPRINT",FACE,{"disambiguationData":[TD([[makeQuery(id+"F0.imprint","IMPRINT",EDGE,{"disambiguationData":[TD([[subQ8,-1.0]])],"derivedFrom":subQ7}),-1.0]])]});}
            var Q42;
            {var subQ3=sQuery(id+"F0.wireOp",EDGE,"E4.104.0");var subQ7=sQuery(id+"F0.wireOp",EDGE,"E1");var subQ8=makeQuery(id+"F0.imprint","INTERSECT",VERTEX,{"derivedFrom":[subQ7,subQ3]});Q42=makeQuery(id+"F0.imprint","IMPRINT",FACE,{"disambiguationData":[TD([[makeQuery(id+"F0.imprint","IMPRINT",EDGE,{"disambiguationData":[TD([[subQ8,-1.0]])],"derivedFrom":subQ7}),-1.0]])]});}
            var Q43;
            {var subQ5=sQuery(id+"F0.wireOp",EDGE,"E4.105.0");var subQ6=sQuery(id+"F0.wireOp",EDGE,"E1");var subQ7=makeQuery(id+"F0.imprint","INTERSECT",VERTEX,{"derivedFrom":[subQ6,subQ5]});Q43=makeQuery(id+"F0.imprint","IMPRINT",FACE,{"disambiguationData":[TD([[makeQuery(id+"F0.imprint","IMPRINT",EDGE,{"disambiguationData":[TD([[subQ7,-1.0]])],"derivedFrom":subQ6}),-1.0]])]});}
            var Q44;
            {var subQ3=sQuery(id+"F0.wireOp",EDGE,"E4.106.0");var subQ7=sQuery(id+"F0.wireOp",EDGE,"E1");var subQ8=makeQuery(id+"F0.imprint","INTERSECT",VERTEX,{"derivedFrom":[subQ7,subQ3]});Q44=makeQuery(id+"F0.imprint","IMPRINT",FACE,{"disambiguationData":[TD([[makeQuery(id+"F0.imprint","IMPRINT",EDGE,{"disambiguationData":[TD([[subQ8,-1.0]])],"derivedFrom":subQ7}),-1.0]])]});}
            var Q45;
            {var subQ3=sQuery(id+"F0.wireOp",EDGE,"E4.107.0");var subQ7=sQuery(id+"F0.wireOp",EDGE,"E1");var subQ8=makeQuery(id+"F0.imprint","INTERSECT",VERTEX,{"derivedFrom":[subQ7,subQ3]});Q45=makeQuery(id+"F0.imprint","IMPRINT",FACE,{"disambiguationData":[TD([[makeQuery(id+"F0.imprint","IMPRINT",EDGE,{"disambiguationData":[TD([[subQ8,-1.0]])],"derivedFrom":subQ7}),-1.0]])]});}
            var Q46;
            {var subQ0=sQuery(id+"F0.wireOp",EDGE,"E3");var subQ1=sQuery(id+"F0.wireOp",EDGE,"E1");var subQ2=makeQuery(id+"F0.imprint","INTERSECT",VERTEX,{"derivedFrom":[subQ1,subQ0]});Q46=makeQuery(id+"F0.imprint","IMPRINT",FACE,{"disambiguationData":[TD([[makeQuery(id+"F0.imprint","IMPRINT",EDGE,{"disambiguationData":[TD([[subQ2,1.0]])],"derivedFrom":subQ1}),-1.0]])]});}
            var Q47;
            {var subQ0=sQuery(id+"F0.wireOp",EDGE,"E4.1.1");var subQ1=sQuery(id+"F0.wireOp",EDGE,"E1");var subQ2=makeQuery(id+"F0.imprint","INTERSECT",VERTEX,{"derivedFrom":[subQ1,subQ0]});Q47=makeQuery(id+"F0.imprint","IMPRINT",FACE,{"disambiguationData":[TD([[makeQuery(id+"F0.imprint","IMPRINT",EDGE,{"disambiguationData":[TD([[subQ2,1.0]])],"derivedFrom":subQ1}),-1.0]])]});}
            var Q48;
            {var subQ5=sQuery(id+"F0.wireOp",EDGE,"E2");var subQ6=sQuery(id+"F0.wireOp",EDGE,"E1");var subQ7=makeQuery(id+"F0.imprint","INTERSECT",VERTEX,{"derivedFrom":[subQ6,subQ5]});Q48=makeQuery(id+"F0.imprint","IMPRINT",FACE,{"disambiguationData":[TD([[makeQuery(id+"F0.imprint","IMPRINT",EDGE,{"disambiguationData":[TD([[subQ7,-1.0]])],"derivedFrom":subQ6}),-1.0]])]});}
            var Q49;
            {var subQ3=sQuery(id+"F0.wireOp",EDGE,"E4.1.0");var subQ7=sQuery(id+"F0.wireOp",EDGE,"E1");var subQ8=makeQuery(id+"F0.imprint","INTERSECT",VERTEX,{"derivedFrom":[subQ7,subQ3]});Q49=makeQuery(id+"F0.imprint","IMPRINT",FACE,{"disambiguationData":[TD([[makeQuery(id+"F0.imprint","IMPRINT",EDGE,{"disambiguationData":[TD([[subQ8,-1.0]])],"derivedFrom":subQ7}),-1.0]])]});}
            var Q50;
            {var subQ3=sQuery(id+"F0.wireOp",EDGE,"E4.2.0");var subQ7=sQuery(id+"F0.wireOp",EDGE,"E1");var subQ8=makeQuery(id+"F0.imprint","INTERSECT",VERTEX,{"derivedFrom":[subQ7,subQ3]});Q50=makeQuery(id+"F0.imprint","IMPRINT",FACE,{"disambiguationData":[TD([[makeQuery(id+"F0.imprint","IMPRINT",EDGE,{"disambiguationData":[TD([[subQ8,-1.0]])],"derivedFrom":subQ7}),-1.0]])]});}
            var Q51;
            {var subQ3=sQuery(id+"F0.wireOp",EDGE,"E4.3.0");var subQ5=sQuery(id+"F0.wireOp",EDGE,"E1");var subQ6=makeQuery(id+"F0.imprint","INTERSECT",VERTEX,{"derivedFrom":[subQ5,subQ3]});Q51=makeQuery(id+"F0.imprint","IMPRINT",FACE,{"disambiguationData":[TD([[makeQuery(id+"F0.imprint","IMPRINT",EDGE,{"disambiguationData":[TD([[subQ6,-1.0]])],"derivedFrom":subQ5}),-1.0]])]});}
            var Q52;
            {var subQ3=sQuery(id+"F0.wireOp",EDGE,"E4.4.0");var subQ7=sQuery(id+"F0.wireOp",EDGE,"E1");var subQ8=makeQuery(id+"F0.imprint","INTERSECT",VERTEX,{"derivedFrom":[subQ7,subQ3]});Q52=makeQuery(id+"F0.imprint","IMPRINT",FACE,{"disambiguationData":[TD([[makeQuery(id+"F0.imprint","IMPRINT",EDGE,{"disambiguationData":[TD([[subQ8,-1.0]])],"derivedFrom":subQ7}),-1.0]])]});}
            var Q53;
            {var subQ3=sQuery(id+"F0.wireOp",EDGE,"E4.17.0");var subQ7=sQuery(id+"F0.wireOp",EDGE,"E1");var subQ8=makeQuery(id+"F0.imprint","INTERSECT",VERTEX,{"derivedFrom":[subQ7,subQ3]});Q53=makeQuery(id+"F0.imprint","IMPRINT",FACE,{"disambiguationData":[TD([[makeQuery(id+"F0.imprint","IMPRINT",EDGE,{"disambiguationData":[TD([[subQ8,-1.0]])],"derivedFrom":subQ7}),-1.0]])]});}
            var Q54;
            {var subQ3=sQuery(id+"F0.wireOp",EDGE,"E4.18.0");var subQ7=sQuery(id+"F0.wireOp",EDGE,"E1");var subQ8=makeQuery(id+"F0.imprint","INTERSECT",VERTEX,{"derivedFrom":[subQ7,subQ3]});Q54=makeQuery(id+"F0.imprint","IMPRINT",FACE,{"disambiguationData":[TD([[makeQuery(id+"F0.imprint","IMPRINT",EDGE,{"disambiguationData":[TD([[subQ8,-1.0]])],"derivedFrom":subQ7}),-1.0]])]});}
            var Q55;
            {var subQ3=sQuery(id+"F0.wireOp",EDGE,"E4.19.0");var subQ7=sQuery(id+"F0.wireOp",EDGE,"E1");var subQ8=makeQuery(id+"F0.imprint","INTERSECT",VERTEX,{"derivedFrom":[subQ7,subQ3]});Q55=makeQuery(id+"F0.imprint","IMPRINT",FACE,{"disambiguationData":[TD([[makeQuery(id+"F0.imprint","IMPRINT",EDGE,{"disambiguationData":[TD([[subQ8,-1.0]])],"derivedFrom":subQ7}),-1.0]])]});}
            var Q56;
            {var subQ0=sQuery(id+"F0.wireOp",EDGE,"E4.20.0");var subQ1=sQuery(id+"F0.wireOp",EDGE,"E1");var subQ2=makeQuery(id+"F0.imprint","INTERSECT",VERTEX,{"derivedFrom":[subQ1,subQ0]});Q56=makeQuery(id+"F0.imprint","IMPRINT",FACE,{"disambiguationData":[TD([[makeQuery(id+"F0.imprint","IMPRINT",EDGE,{"disambiguationData":[TD([[subQ2,1.0]])],"derivedFrom":subQ1}),-1.0]])]});}
            var Q57;
            {var subQ3=sQuery(id+"F0.wireOp",EDGE,"E4.21.0");var subQ7=sQuery(id+"F0.wireOp",EDGE,"E1");var subQ8=makeQuery(id+"F0.imprint","INTERSECT",VERTEX,{"derivedFrom":[subQ7,subQ3]});Q57=makeQuery(id+"F0.imprint","IMPRINT",FACE,{"disambiguationData":[TD([[makeQuery(id+"F0.imprint","IMPRINT",EDGE,{"disambiguationData":[TD([[subQ8,-1.0]])],"derivedFrom":subQ7}),-1.0]])]});}
            var Q58;
            {var subQ3=sQuery(id+"F0.wireOp",EDGE,"E4.22.0");var subQ7=sQuery(id+"F0.wireOp",EDGE,"E1");var subQ8=makeQuery(id+"F0.imprint","INTERSECT",VERTEX,{"derivedFrom":[subQ7,subQ3]});Q58=makeQuery(id+"F0.imprint","IMPRINT",FACE,{"disambiguationData":[TD([[makeQuery(id+"F0.imprint","IMPRINT",EDGE,{"disambiguationData":[TD([[subQ8,-1.0]])],"derivedFrom":subQ7}),-1.0]])]});}
            var Q59;
            {var subQ3=sQuery(id+"F0.wireOp",EDGE,"E4.26.0");var subQ7=sQuery(id+"F0.wireOp",EDGE,"E1");var subQ8=makeQuery(id+"F0.imprint","INTERSECT",VERTEX,{"derivedFrom":[subQ7,subQ3]});Q59=makeQuery(id+"F0.imprint","IMPRINT",FACE,{"disambiguationData":[TD([[makeQuery(id+"F0.imprint","IMPRINT",EDGE,{"disambiguationData":[TD([[subQ8,-1.0]])],"derivedFrom":subQ7}),-1.0]])]});}
            var Q60;
            {var subQ3=sQuery(id+"F0.wireOp",EDGE,"E4.27.0");var subQ7=sQuery(id+"F0.wireOp",EDGE,"E1");var subQ8=makeQuery(id+"F0.imprint","INTERSECT",VERTEX,{"derivedFrom":[subQ7,subQ3]});Q60=makeQuery(id+"F0.imprint","IMPRINT",FACE,{"disambiguationData":[TD([[makeQuery(id+"F0.imprint","IMPRINT",EDGE,{"disambiguationData":[TD([[subQ8,-1.0]])],"derivedFrom":subQ7}),-1.0]])]});}
            var Q61;
            {var subQ3=sQuery(id+"F0.wireOp",EDGE,"E4.24.0");var subQ7=sQuery(id+"F0.wireOp",EDGE,"E1");var subQ8=makeQuery(id+"F0.imprint","INTERSECT",VERTEX,{"derivedFrom":[subQ7,subQ3]});Q61=makeQuery(id+"F0.imprint","IMPRINT",FACE,{"disambiguationData":[TD([[makeQuery(id+"F0.imprint","IMPRINT",EDGE,{"disambiguationData":[TD([[subQ8,-1.0]])],"derivedFrom":subQ7}),-1.0]])]});}
            var Q62;
            {var subQ3=sQuery(id+"F0.wireOp",EDGE,"E4.23.0");var subQ7=sQuery(id+"F0.wireOp",EDGE,"E1");var subQ8=makeQuery(id+"F0.imprint","INTERSECT",VERTEX,{"derivedFrom":[subQ7,subQ3]});Q62=makeQuery(id+"F0.imprint","IMPRINT",FACE,{"disambiguationData":[TD([[makeQuery(id+"F0.imprint","IMPRINT",EDGE,{"disambiguationData":[TD([[subQ8,-1.0]])],"derivedFrom":subQ7}),-1.0]])]});}
            var Q63;
            {var subQ3=sQuery(id+"F0.wireOp",EDGE,"E4.16.0");var subQ7=sQuery(id+"F0.wireOp",EDGE,"E1");var subQ8=makeQuery(id+"F0.imprint","INTERSECT",VERTEX,{"derivedFrom":[subQ7,subQ3]});Q63=makeQuery(id+"F0.imprint","IMPRINT",FACE,{"disambiguationData":[TD([[makeQuery(id+"F0.imprint","IMPRINT",EDGE,{"disambiguationData":[TD([[subQ8,-1.0]])],"derivedFrom":subQ7}),-1.0]])]});}
            var Q64;
            {var subQ5=sQuery(id+"F0.wireOp",EDGE,"E4.15.0");var subQ6=sQuery(id+"F0.wireOp",EDGE,"E1");var subQ7=makeQuery(id+"F0.imprint","INTERSECT",VERTEX,{"derivedFrom":[subQ6,subQ5]});Q64=makeQuery(id+"F0.imprint","IMPRINT",FACE,{"disambiguationData":[TD([[makeQuery(id+"F0.imprint","IMPRINT",EDGE,{"disambiguationData":[TD([[subQ7,-1.0]])],"derivedFrom":subQ6}),-1.0]])]});}
            var Q65;
            {var subQ3=sQuery(id+"F0.wireOp",EDGE,"E4.14.0");var subQ5=sQuery(id+"F0.wireOp",EDGE,"E1");var subQ6=makeQuery(id+"F0.imprint","INTERSECT",VERTEX,{"derivedFrom":[subQ5,subQ3]});Q65=makeQuery(id+"F0.imprint","IMPRINT",FACE,{"disambiguationData":[TD([[makeQuery(id+"F0.imprint","IMPRINT",EDGE,{"disambiguationData":[TD([[subQ6,-1.0]])],"derivedFrom":subQ5}),-1.0]])]});}
            var Q66;
            {var subQ0=sQuery(id+"F0.wireOp",EDGE,"E4.13.0");var subQ1=sQuery(id+"F0.wireOp",EDGE,"E1");var subQ2=makeQuery(id+"F0.imprint","INTERSECT",VERTEX,{"derivedFrom":[subQ1,subQ0]});Q66=makeQuery(id+"F0.imprint","IMPRINT",FACE,{"disambiguationData":[TD([[makeQuery(id+"F0.imprint","IMPRINT",EDGE,{"disambiguationData":[TD([[subQ2,1.0]])],"derivedFrom":subQ1}),-1.0]])]});}
            var Q67;
            {var subQ3=sQuery(id+"F0.wireOp",EDGE,"E4.11.0");var subQ7=sQuery(id+"F0.wireOp",EDGE,"E1");var subQ8=makeQuery(id+"F0.imprint","INTERSECT",VERTEX,{"derivedFrom":[subQ7,subQ3]});Q67=makeQuery(id+"F0.imprint","IMPRINT",FACE,{"disambiguationData":[TD([[makeQuery(id+"F0.imprint","IMPRINT",EDGE,{"disambiguationData":[TD([[subQ8,-1.0]])],"derivedFrom":subQ7}),-1.0]])]});}
            var Q68;
            {var subQ5=sQuery(id+"F0.wireOp",EDGE,"E4.10.0");var subQ6=sQuery(id+"F0.wireOp",EDGE,"E1");var subQ7=makeQuery(id+"F0.imprint","INTERSECT",VERTEX,{"derivedFrom":[subQ6,subQ5]});Q68=makeQuery(id+"F0.imprint","IMPRINT",FACE,{"disambiguationData":[TD([[makeQuery(id+"F0.imprint","IMPRINT",EDGE,{"disambiguationData":[TD([[subQ7,-1.0]])],"derivedFrom":subQ6}),-1.0]])]});}
            var Q69;
            {var subQ3=sQuery(id+"F0.wireOp",EDGE,"E4.9.0");var subQ7=sQuery(id+"F0.wireOp",EDGE,"E1");var subQ8=makeQuery(id+"F0.imprint","INTERSECT",VERTEX,{"derivedFrom":[subQ7,subQ3]});Q69=makeQuery(id+"F0.imprint","IMPRINT",FACE,{"disambiguationData":[TD([[makeQuery(id+"F0.imprint","IMPRINT",EDGE,{"disambiguationData":[TD([[subQ8,-1.0]])],"derivedFrom":subQ7}),-1.0]])]});}
            var Q70;
            {var subQ3=sQuery(id+"F0.wireOp",EDGE,"E4.8.0");var subQ7=sQuery(id+"F0.wireOp",EDGE,"E1");var subQ8=makeQuery(id+"F0.imprint","INTERSECT",VERTEX,{"derivedFrom":[subQ7,subQ3]});Q70=makeQuery(id+"F0.imprint","IMPRINT",FACE,{"disambiguationData":[TD([[makeQuery(id+"F0.imprint","IMPRINT",EDGE,{"disambiguationData":[TD([[subQ8,-1.0]])],"derivedFrom":subQ7}),-1.0]])]});}
            var Q71;
            {var subQ3=sQuery(id+"F0.wireOp",EDGE,"E4.7.0");var subQ7=sQuery(id+"F0.wireOp",EDGE,"E1");var subQ8=makeQuery(id+"F0.imprint","INTERSECT",VERTEX,{"derivedFrom":[subQ7,subQ3]});Q71=makeQuery(id+"F0.imprint","IMPRINT",FACE,{"disambiguationData":[TD([[makeQuery(id+"F0.imprint","IMPRINT",EDGE,{"disambiguationData":[TD([[subQ8,-1.0]])],"derivedFrom":subQ7}),-1.0]])]});}
            var Q72;
            {var subQ3=sQuery(id+"F0.wireOp",EDGE,"E4.6.0");var subQ7=sQuery(id+"F0.wireOp",EDGE,"E1");var subQ8=makeQuery(id+"F0.imprint","INTERSECT",VERTEX,{"derivedFrom":[subQ7,subQ3]});Q72=makeQuery(id+"F0.imprint","IMPRINT",FACE,{"disambiguationData":[TD([[makeQuery(id+"F0.imprint","IMPRINT",EDGE,{"disambiguationData":[TD([[subQ8,-1.0]])],"derivedFrom":subQ7}),-1.0]])]});}
            var Q73;
            {var subQ5=sQuery(id+"F0.wireOp",EDGE,"E4.5.0");var subQ6=sQuery(id+"F0.wireOp",EDGE,"E1");var subQ7=makeQuery(id+"F0.imprint","INTERSECT",VERTEX,{"derivedFrom":[subQ6,subQ5]});Q73=makeQuery(id+"F0.imprint","IMPRINT",FACE,{"disambiguationData":[TD([[makeQuery(id+"F0.imprint","IMPRINT",EDGE,{"disambiguationData":[TD([[subQ7,-1.0]])],"derivedFrom":subQ6}),-1.0]])]});}
            var Q74;
            {var subQ3=sQuery(id+"F0.wireOp",EDGE,"E4.89.0");var subQ7=sQuery(id+"F0.wireOp",EDGE,"E1");var subQ8=makeQuery(id+"F0.imprint","INTERSECT",VERTEX,{"derivedFrom":[subQ7,subQ3]});Q74=makeQuery(id+"F0.imprint","IMPRINT",FACE,{"disambiguationData":[TD([[makeQuery(id+"F0.imprint","IMPRINT",EDGE,{"disambiguationData":[TD([[subQ8,-1.0]])],"derivedFrom":subQ7}),-1.0]])]});}
            var Q75;
            {var subQ3=sQuery(id+"F0.wireOp",EDGE,"E4.78.0");var subQ7=sQuery(id+"F0.wireOp",EDGE,"E1");var subQ8=makeQuery(id+"F0.imprint","INTERSECT",VERTEX,{"derivedFrom":[subQ7,subQ3]});Q75=makeQuery(id+"F0.imprint","IMPRINT",FACE,{"disambiguationData":[TD([[makeQuery(id+"F0.imprint","IMPRINT",EDGE,{"disambiguationData":[TD([[subQ8,-1.0]])],"derivedFrom":subQ7}),-1.0]])]});}
            var Q76;
            {var subQ3=sQuery(id+"F0.wireOp",EDGE,"E4.77.0");var subQ7=sQuery(id+"F0.wireOp",EDGE,"E1");var subQ8=makeQuery(id+"F0.imprint","INTERSECT",VERTEX,{"derivedFrom":[subQ7,subQ3]});Q76=makeQuery(id+"F0.imprint","IMPRINT",FACE,{"disambiguationData":[TD([[makeQuery(id+"F0.imprint","IMPRINT",EDGE,{"disambiguationData":[TD([[subQ8,-1.0]])],"derivedFrom":subQ7}),-1.0]])]});}
            var Q77;
            {var subQ3=sQuery(id+"F0.wireOp",EDGE,"E4.87.0");var subQ7=sQuery(id+"F0.wireOp",EDGE,"E1");var subQ8=makeQuery(id+"F0.imprint","INTERSECT",VERTEX,{"derivedFrom":[subQ7,subQ3]});Q77=makeQuery(id+"F0.imprint","IMPRINT",FACE,{"disambiguationData":[TD([[makeQuery(id+"F0.imprint","IMPRINT",EDGE,{"disambiguationData":[TD([[subQ8,-1.0]])],"derivedFrom":subQ7}),-1.0]])]});}
            var Q78;
            {var subQ3=sQuery(id+"F0.wireOp",EDGE,"E4.86.0");var subQ7=sQuery(id+"F0.wireOp",EDGE,"E1");var subQ8=makeQuery(id+"F0.imprint","INTERSECT",VERTEX,{"derivedFrom":[subQ7,subQ3]});Q78=makeQuery(id+"F0.imprint","IMPRINT",FACE,{"disambiguationData":[TD([[makeQuery(id+"F0.imprint","IMPRINT",EDGE,{"disambiguationData":[TD([[subQ8,-1.0]])],"derivedFrom":subQ7}),-1.0]])]});}
            var Q79;
            {var subQ5=sQuery(id+"F0.wireOp",EDGE,"E4.85.0");var subQ6=sQuery(id+"F0.wireOp",EDGE,"E1");var subQ7=makeQuery(id+"F0.imprint","INTERSECT",VERTEX,{"derivedFrom":[subQ6,subQ5]});Q79=makeQuery(id+"F0.imprint","IMPRINT",FACE,{"disambiguationData":[TD([[makeQuery(id+"F0.imprint","IMPRINT",EDGE,{"disambiguationData":[TD([[subQ7,-1.0]])],"derivedFrom":subQ6}),-1.0]])]});}
            var Q80;
            {var subQ3=sQuery(id+"F0.wireOp",EDGE,"E4.74.0");var subQ7=sQuery(id+"F0.wireOp",EDGE,"E1");var subQ8=makeQuery(id+"F0.imprint","INTERSECT",VERTEX,{"derivedFrom":[subQ7,subQ3]});Q80=makeQuery(id+"F0.imprint","IMPRINT",FACE,{"disambiguationData":[TD([[makeQuery(id+"F0.imprint","IMPRINT",EDGE,{"disambiguationData":[TD([[subQ8,-1.0]])],"derivedFrom":subQ7}),-1.0]])]});}
            var Q81;
            {var subQ3=sQuery(id+"F0.wireOp",EDGE,"E4.84.0");var subQ7=sQuery(id+"F0.wireOp",EDGE,"E1");var subQ8=makeQuery(id+"F0.imprint","INTERSECT",VERTEX,{"derivedFrom":[subQ7,subQ3]});Q81=makeQuery(id+"F0.imprint","IMPRINT",FACE,{"disambiguationData":[TD([[makeQuery(id+"F0.imprint","IMPRINT",EDGE,{"disambiguationData":[TD([[subQ8,-1.0]])],"derivedFrom":subQ7}),-1.0]])]});}
            var Q82;
            {var subQ3=sQuery(id+"F0.wireOp",EDGE,"E4.83.0");var subQ7=sQuery(id+"F0.wireOp",EDGE,"E1");var subQ8=makeQuery(id+"F0.imprint","INTERSECT",VERTEX,{"derivedFrom":[subQ7,subQ3]});Q82=makeQuery(id+"F0.imprint","IMPRINT",FACE,{"disambiguationData":[TD([[makeQuery(id+"F0.imprint","IMPRINT",EDGE,{"disambiguationData":[TD([[subQ8,-1.0]])],"derivedFrom":subQ7}),-1.0]])]});}
            var Q83;
            {var subQ3=sQuery(id+"F0.wireOp",EDGE,"E4.39.0");var subQ7=sQuery(id+"F0.wireOp",EDGE,"E1");var subQ8=makeQuery(id+"F0.imprint","INTERSECT",VERTEX,{"derivedFrom":[subQ7,subQ3]});Q83=makeQuery(id+"F0.imprint","IMPRINT",FACE,{"disambiguationData":[TD([[makeQuery(id+"F0.imprint","IMPRINT",EDGE,{"disambiguationData":[TD([[subQ8,-1.0]])],"derivedFrom":subQ7}),-1.0]])]});}
            var Q84;
            {var subQ3=sQuery(id+"F0.wireOp",EDGE,"E4.38.0");var subQ7=sQuery(id+"F0.wireOp",EDGE,"E1");var subQ8=makeQuery(id+"F0.imprint","INTERSECT",VERTEX,{"derivedFrom":[subQ7,subQ3]});Q84=makeQuery(id+"F0.imprint","IMPRINT",FACE,{"disambiguationData":[TD([[makeQuery(id+"F0.imprint","IMPRINT",EDGE,{"disambiguationData":[TD([[subQ8,-1.0]])],"derivedFrom":subQ7}),-1.0]])]});}
            var Q85;
            {var subQ3=sQuery(id+"F0.wireOp",EDGE,"E4.37.0");var subQ7=sQuery(id+"F0.wireOp",EDGE,"E1");var subQ8=makeQuery(id+"F0.imprint","INTERSECT",VERTEX,{"derivedFrom":[subQ7,subQ3]});Q85=makeQuery(id+"F0.imprint","IMPRINT",FACE,{"disambiguationData":[TD([[makeQuery(id+"F0.imprint","IMPRINT",EDGE,{"disambiguationData":[TD([[subQ8,-1.0]])],"derivedFrom":subQ7}),-1.0]])]});}
            var Q86;
            {var subQ3=sQuery(id+"F0.wireOp",EDGE,"E4.36.0");var subQ5=sQuery(id+"F0.wireOp",EDGE,"E1");var subQ6=makeQuery(id+"F0.imprint","INTERSECT",VERTEX,{"derivedFrom":[subQ5,subQ3]});Q86=makeQuery(id+"F0.imprint","IMPRINT",FACE,{"disambiguationData":[TD([[makeQuery(id+"F0.imprint","IMPRINT",EDGE,{"disambiguationData":[TD([[subQ6,-1.0]])],"derivedFrom":subQ5}),-1.0]])]});}
            var Q87;
            {var subQ5=sQuery(id+"F0.wireOp",EDGE,"E4.35.0");var subQ6=sQuery(id+"F0.wireOp",EDGE,"E1");var subQ7=makeQuery(id+"F0.imprint","INTERSECT",VERTEX,{"derivedFrom":[subQ6,subQ5]});Q87=makeQuery(id+"F0.imprint","IMPRINT",FACE,{"disambiguationData":[TD([[makeQuery(id+"F0.imprint","IMPRINT",EDGE,{"disambiguationData":[TD([[subQ7,-1.0]])],"derivedFrom":subQ6}),-1.0]])]});}
            var Q88;
            {var subQ0=sQuery(id+"F0.wireOp",EDGE,"E4.35.0");var subQ1=sQuery(id+"F0.wireOp",EDGE,"E1");var subQ2=makeQuery(id+"F0.imprint","INTERSECT",VERTEX,{"derivedFrom":[subQ1,subQ0]});Q88=makeQuery(id+"F0.imprint","IMPRINT",FACE,{"disambiguationData":[TD([[makeQuery(id+"F0.imprint","IMPRINT",EDGE,{"disambiguationData":[TD([[subQ2,1.0]])],"derivedFrom":subQ1}),-1.0]])]});}
            var Q89;
            {var subQ3=sQuery(id+"F0.wireOp",EDGE,"E4.33.0");var subQ7=sQuery(id+"F0.wireOp",EDGE,"E1");var subQ8=makeQuery(id+"F0.imprint","INTERSECT",VERTEX,{"derivedFrom":[subQ7,subQ3]});Q89=makeQuery(id+"F0.imprint","IMPRINT",FACE,{"disambiguationData":[TD([[makeQuery(id+"F0.imprint","IMPRINT",EDGE,{"disambiguationData":[TD([[subQ8,-1.0]])],"derivedFrom":subQ7}),-1.0]])]});}
            var Q90;
            {var subQ3=sQuery(id+"F0.wireOp",EDGE,"E4.32.0");var subQ7=sQuery(id+"F0.wireOp",EDGE,"E1");var subQ8=makeQuery(id+"F0.imprint","INTERSECT",VERTEX,{"derivedFrom":[subQ7,subQ3]});Q90=makeQuery(id+"F0.imprint","IMPRINT",FACE,{"disambiguationData":[TD([[makeQuery(id+"F0.imprint","IMPRINT",EDGE,{"disambiguationData":[TD([[subQ8,-1.0]])],"derivedFrom":subQ7}),-1.0]])]});}
            var Q91;
            {var subQ3=sQuery(id+"F0.wireOp",EDGE,"E4.31.0");var subQ7=sQuery(id+"F0.wireOp",EDGE,"E1");var subQ8=makeQuery(id+"F0.imprint","INTERSECT",VERTEX,{"derivedFrom":[subQ7,subQ3]});Q91=makeQuery(id+"F0.imprint","IMPRINT",FACE,{"disambiguationData":[TD([[makeQuery(id+"F0.imprint","IMPRINT",EDGE,{"disambiguationData":[TD([[subQ8,-1.0]])],"derivedFrom":subQ7}),-1.0]])]});}
            var Q92;
            {var subQ5=sQuery(id+"F0.wireOp",EDGE,"E4.30.0");var subQ6=sQuery(id+"F0.wireOp",EDGE,"E1");var subQ7=makeQuery(id+"F0.imprint","INTERSECT",VERTEX,{"derivedFrom":[subQ6,subQ5]});Q92=makeQuery(id+"F0.imprint","IMPRINT",FACE,{"disambiguationData":[TD([[makeQuery(id+"F0.imprint","IMPRINT",EDGE,{"disambiguationData":[TD([[subQ7,-1.0]])],"derivedFrom":subQ6}),-1.0]])]});}
            var Q93;
            {var subQ3=sQuery(id+"F0.wireOp",EDGE,"E4.72.0");var subQ7=sQuery(id+"F0.wireOp",EDGE,"E1");var subQ8=makeQuery(id+"F0.imprint","INTERSECT",VERTEX,{"derivedFrom":[subQ7,subQ3]});Q93=makeQuery(id+"F0.imprint","IMPRINT",FACE,{"disambiguationData":[TD([[makeQuery(id+"F0.imprint","IMPRINT",EDGE,{"disambiguationData":[TD([[subQ8,-1.0]])],"derivedFrom":subQ7}),-1.0]])]});}
            var Q94;
            {var subQ5=sQuery(id+"F0.wireOp",EDGE,"E4.50.0");var subQ6=sQuery(id+"F0.wireOp",EDGE,"E1");var subQ7=makeQuery(id+"F0.imprint","INTERSECT",VERTEX,{"derivedFrom":[subQ6,subQ5]});Q94=makeQuery(id+"F0.imprint","IMPRINT",FACE,{"disambiguationData":[TD([[makeQuery(id+"F0.imprint","IMPRINT",EDGE,{"disambiguationData":[TD([[subQ7,-1.0]])],"derivedFrom":subQ6}),-1.0]])]});}
            var Q95;
            {var subQ3=sQuery(id+"F0.wireOp",EDGE,"E4.49.0");var subQ7=sQuery(id+"F0.wireOp",EDGE,"E1");var subQ8=makeQuery(id+"F0.imprint","INTERSECT",VERTEX,{"derivedFrom":[subQ7,subQ3]});Q95=makeQuery(id+"F0.imprint","IMPRINT",FACE,{"disambiguationData":[TD([[makeQuery(id+"F0.imprint","IMPRINT",EDGE,{"disambiguationData":[TD([[subQ8,-1.0]])],"derivedFrom":subQ7}),-1.0]])]});}
            var Q96;
            {var subQ3=sQuery(id+"F0.wireOp",EDGE,"E4.46.0");var subQ7=sQuery(id+"F0.wireOp",EDGE,"E1");var subQ8=makeQuery(id+"F0.imprint","INTERSECT",VERTEX,{"derivedFrom":[subQ7,subQ3]});Q96=makeQuery(id+"F0.imprint","IMPRINT",FACE,{"disambiguationData":[TD([[makeQuery(id+"F0.imprint","IMPRINT",EDGE,{"disambiguationData":[TD([[subQ8,-1.0]])],"derivedFrom":subQ7}),-1.0]])]});}
            var Q97;
            {var subQ3=sQuery(id+"F0.wireOp",EDGE,"E4.48.0");var subQ7=sQuery(id+"F0.wireOp",EDGE,"E1");var subQ8=makeQuery(id+"F0.imprint","INTERSECT",VERTEX,{"derivedFrom":[subQ7,subQ3]});Q97=makeQuery(id+"F0.imprint","IMPRINT",FACE,{"disambiguationData":[TD([[makeQuery(id+"F0.imprint","IMPRINT",EDGE,{"disambiguationData":[TD([[subQ8,-1.0]])],"derivedFrom":subQ7}),-1.0]])]});}
            var Q98;
            {var subQ3=sQuery(id+"F0.wireOp",EDGE,"E4.82.0");var subQ7=sQuery(id+"F0.wireOp",EDGE,"E1");var subQ8=makeQuery(id+"F0.imprint","INTERSECT",VERTEX,{"derivedFrom":[subQ7,subQ3]});Q98=makeQuery(id+"F0.imprint","IMPRINT",FACE,{"disambiguationData":[TD([[makeQuery(id+"F0.imprint","IMPRINT",EDGE,{"disambiguationData":[TD([[subQ8,-1.0]])],"derivedFrom":subQ7}),-1.0]])]});}
            var Q99;
            {var subQ3=sQuery(id+"F0.wireOp",EDGE,"E4.47.0");var subQ5=sQuery(id+"F0.wireOp",EDGE,"E1");var subQ6=makeQuery(id+"F0.imprint","INTERSECT",VERTEX,{"derivedFrom":[subQ5,subQ3]});Q99=makeQuery(id+"F0.imprint","IMPRINT",FACE,{"disambiguationData":[TD([[makeQuery(id+"F0.imprint","IMPRINT",EDGE,{"disambiguationData":[TD([[subQ6,-1.0]])],"derivedFrom":subQ5}),-1.0]])]});}
            var Q100;
            {var subQ3=sQuery(id+"F0.wireOp",EDGE,"E4.71.0");var subQ7=sQuery(id+"F0.wireOp",EDGE,"E1");var subQ8=makeQuery(id+"F0.imprint","INTERSECT",VERTEX,{"derivedFrom":[subQ7,subQ3]});Q100=makeQuery(id+"F0.imprint","IMPRINT",FACE,{"disambiguationData":[TD([[makeQuery(id+"F0.imprint","IMPRINT",EDGE,{"disambiguationData":[TD([[subQ8,-1.0]])],"derivedFrom":subQ7}),-1.0]])]});}
            var Q101;
            {var subQ3=sQuery(id+"F0.wireOp",EDGE,"E4.28.0");var subQ7=sQuery(id+"F0.wireOp",EDGE,"E1");var subQ8=makeQuery(id+"F0.imprint","INTERSECT",VERTEX,{"derivedFrom":[subQ7,subQ3]});Q101=makeQuery(id+"F0.imprint","IMPRINT",FACE,{"disambiguationData":[TD([[makeQuery(id+"F0.imprint","IMPRINT",EDGE,{"disambiguationData":[TD([[subQ8,-1.0]])],"derivedFrom":subQ7}),-1.0]])]});}
            var Q102;
            {var subQ0=sQuery(id+"F0.wireOp",EDGE,"E4.42.0");var subQ1=sQuery(id+"F0.wireOp",EDGE,"E1");var subQ2=makeQuery(id+"F0.imprint","INTERSECT",VERTEX,{"derivedFrom":[subQ1,subQ0]});Q102=makeQuery(id+"F0.imprint","IMPRINT",FACE,{"disambiguationData":[TD([[makeQuery(id+"F0.imprint","IMPRINT",EDGE,{"disambiguationData":[TD([[subQ2,1.0]])],"derivedFrom":subQ1}),-1.0]])]});}
            var Q103;
            {var subQ5=sQuery(id+"F0.wireOp",EDGE,"E4.40.0");var subQ6=sQuery(id+"F0.wireOp",EDGE,"E1");var subQ7=makeQuery(id+"F0.imprint","INTERSECT",VERTEX,{"derivedFrom":[subQ6,subQ5]});Q103=makeQuery(id+"F0.imprint","IMPRINT",FACE,{"disambiguationData":[TD([[makeQuery(id+"F0.imprint","IMPRINT",EDGE,{"disambiguationData":[TD([[subQ7,-1.0]])],"derivedFrom":subQ6}),-1.0]])]});}
            var Q104;
            {var subQ3=sQuery(id+"F0.wireOp",EDGE,"E4.29.0");var subQ7=sQuery(id+"F0.wireOp",EDGE,"E1");var subQ8=makeQuery(id+"F0.imprint","INTERSECT",VERTEX,{"derivedFrom":[subQ7,subQ3]});Q104=makeQuery(id+"F0.imprint","IMPRINT",FACE,{"disambiguationData":[TD([[makeQuery(id+"F0.imprint","IMPRINT",EDGE,{"disambiguationData":[TD([[subQ8,-1.0]])],"derivedFrom":subQ7}),-1.0]])]});}
            var Q105;
            {var subQ3=sQuery(id+"F0.wireOp",EDGE,"E4.56.0");var subQ7=sQuery(id+"F0.wireOp",EDGE,"E1");var subQ8=makeQuery(id+"F0.imprint","INTERSECT",VERTEX,{"derivedFrom":[subQ7,subQ3]});Q105=makeQuery(id+"F0.imprint","IMPRINT",FACE,{"disambiguationData":[TD([[makeQuery(id+"F0.imprint","IMPRINT",EDGE,{"disambiguationData":[TD([[subQ8,-1.0]])],"derivedFrom":subQ7}),-1.0]])]});}
            var Q106;
            {var subQ3=sQuery(id+"F0.wireOp",EDGE,"E4.44.0");var subQ7=sQuery(id+"F0.wireOp",EDGE,"E1");var subQ8=makeQuery(id+"F0.imprint","INTERSECT",VERTEX,{"derivedFrom":[subQ7,subQ3]});Q106=makeQuery(id+"F0.imprint","IMPRINT",FACE,{"disambiguationData":[TD([[makeQuery(id+"F0.imprint","IMPRINT",EDGE,{"disambiguationData":[TD([[subQ8,-1.0]])],"derivedFrom":subQ7}),-1.0]])]});}
            var Q107;
            {var subQ3=sQuery(id+"F0.wireOp",EDGE,"E4.43.0");var subQ7=sQuery(id+"F0.wireOp",EDGE,"E1");var subQ8=makeQuery(id+"F0.imprint","INTERSECT",VERTEX,{"derivedFrom":[subQ7,subQ3]});Q107=makeQuery(id+"F0.imprint","IMPRINT",FACE,{"disambiguationData":[TD([[makeQuery(id+"F0.imprint","IMPRINT",EDGE,{"disambiguationData":[TD([[subQ8,-1.0]])],"derivedFrom":subQ7}),-1.0]])]});}
            var Q108;
            {var subQ3=sQuery(id+"F0.wireOp",EDGE,"E4.51.0");var subQ7=sQuery(id+"F0.wireOp",EDGE,"E1");var subQ8=makeQuery(id+"F0.imprint","INTERSECT",VERTEX,{"derivedFrom":[subQ7,subQ3]});Q108=makeQuery(id+"F0.imprint","IMPRINT",FACE,{"disambiguationData":[TD([[makeQuery(id+"F0.imprint","IMPRINT",EDGE,{"disambiguationData":[TD([[subQ8,-1.0]])],"derivedFrom":subQ7}),-1.0]])]});}
            var Q109;
            {var subQ3=sQuery(id+"F0.wireOp",EDGE,"E4.52.0");var subQ7=sQuery(id+"F0.wireOp",EDGE,"E1");var subQ8=makeQuery(id+"F0.imprint","INTERSECT",VERTEX,{"derivedFrom":[subQ7,subQ3]});Q109=makeQuery(id+"F0.imprint","IMPRINT",FACE,{"disambiguationData":[TD([[makeQuery(id+"F0.imprint","IMPRINT",EDGE,{"disambiguationData":[TD([[subQ8,-1.0]])],"derivedFrom":subQ7}),-1.0]])]});}
            var Q110;
            {var subQ3=sQuery(id+"F0.wireOp",EDGE,"E4.53.0");var subQ7=sQuery(id+"F0.wireOp",EDGE,"E1");var subQ8=makeQuery(id+"F0.imprint","INTERSECT",VERTEX,{"derivedFrom":[subQ7,subQ3]});Q110=makeQuery(id+"F0.imprint","IMPRINT",FACE,{"disambiguationData":[TD([[makeQuery(id+"F0.imprint","IMPRINT",EDGE,{"disambiguationData":[TD([[subQ8,-1.0]])],"derivedFrom":subQ7}),-1.0]])]});}
            var Q111;
            {var subQ3=sQuery(id+"F0.wireOp",EDGE,"E4.54.0");var subQ7=sQuery(id+"F0.wireOp",EDGE,"E1");var subQ8=makeQuery(id+"F0.imprint","INTERSECT",VERTEX,{"derivedFrom":[subQ7,subQ3]});Q111=makeQuery(id+"F0.imprint","IMPRINT",FACE,{"disambiguationData":[TD([[makeQuery(id+"F0.imprint","IMPRINT",EDGE,{"disambiguationData":[TD([[subQ8,-1.0]])],"derivedFrom":subQ7}),-1.0]])]});}
            var Q112;
            {var subQ5=sQuery(id+"F0.wireOp",EDGE,"E4.55.0");var subQ6=sQuery(id+"F0.wireOp",EDGE,"E1");var subQ7=makeQuery(id+"F0.imprint","INTERSECT",VERTEX,{"derivedFrom":[subQ6,subQ5]});Q112=makeQuery(id+"F0.imprint","IMPRINT",FACE,{"disambiguationData":[TD([[makeQuery(id+"F0.imprint","IMPRINT",EDGE,{"disambiguationData":[TD([[subQ7,-1.0]])],"derivedFrom":subQ6}),-1.0]])]});}
            var Q113;
            {var subQ3=sQuery(id+"F0.wireOp",EDGE,"E4.57.0");var subQ7=sQuery(id+"F0.wireOp",EDGE,"E1");var subQ8=makeQuery(id+"F0.imprint","INTERSECT",VERTEX,{"derivedFrom":[subQ7,subQ3]});Q113=makeQuery(id+"F0.imprint","IMPRINT",FACE,{"disambiguationData":[TD([[makeQuery(id+"F0.imprint","IMPRINT",EDGE,{"disambiguationData":[TD([[subQ8,-1.0]])],"derivedFrom":subQ7}),-1.0]])]});}
            var Q114;
            {var subQ3=sQuery(id+"F0.wireOp",EDGE,"E4.58.0");var subQ5=sQuery(id+"F0.wireOp",EDGE,"E1");var subQ6=makeQuery(id+"F0.imprint","INTERSECT",VERTEX,{"derivedFrom":[subQ5,subQ3]});Q114=makeQuery(id+"F0.imprint","IMPRINT",FACE,{"disambiguationData":[TD([[makeQuery(id+"F0.imprint","IMPRINT",EDGE,{"disambiguationData":[TD([[subQ6,-1.0]])],"derivedFrom":subQ5}),-1.0]])]});}
            var Q115;
            {var subQ5=sQuery(id+"F0.wireOp",EDGE,"E4.60.0");var subQ6=sQuery(id+"F0.wireOp",EDGE,"E1");var subQ7=makeQuery(id+"F0.imprint","INTERSECT",VERTEX,{"derivedFrom":[subQ6,subQ5]});Q115=makeQuery(id+"F0.imprint","IMPRINT",FACE,{"disambiguationData":[TD([[makeQuery(id+"F0.imprint","IMPRINT",EDGE,{"disambiguationData":[TD([[subQ7,-1.0]])],"derivedFrom":subQ6}),-1.0]])]});}
            var Q116;
            {var subQ0=sQuery(id+"F0.wireOp",EDGE,"E4.77.0");var subQ1=sQuery(id+"F0.wireOp",EDGE,"E1");var subQ2=makeQuery(id+"F0.imprint","INTERSECT",VERTEX,{"derivedFrom":[subQ1,subQ0]});Q116=makeQuery(id+"F0.imprint","IMPRINT",FACE,{"disambiguationData":[TD([[makeQuery(id+"F0.imprint","IMPRINT",EDGE,{"disambiguationData":[TD([[subQ2,1.0]])],"derivedFrom":subQ1}),-1.0]])]});}
            var Q117;
            {var subQ0=sQuery(id+"F0.wireOp",EDGE,"E4.73.0");var subQ1=sQuery(id+"F0.wireOp",EDGE,"E1");var subQ2=makeQuery(id+"F0.imprint","INTERSECT",VERTEX,{"derivedFrom":[subQ1,subQ0]});Q117=makeQuery(id+"F0.imprint","IMPRINT",FACE,{"disambiguationData":[TD([[makeQuery(id+"F0.imprint","IMPRINT",EDGE,{"disambiguationData":[TD([[subQ2,1.0]])],"derivedFrom":subQ1}),-1.0]])]});}
            var Q118;
            {var subQ0=sQuery(id+"F0.wireOp",EDGE,"E4.70.0");var subQ1=sQuery(id+"F0.wireOp",EDGE,"E1");var subQ2=makeQuery(id+"F0.imprint","INTERSECT",VERTEX,{"derivedFrom":[subQ1,subQ0]});Q118=makeQuery(id+"F0.imprint","IMPRINT",FACE,{"disambiguationData":[TD([[makeQuery(id+"F0.imprint","IMPRINT",EDGE,{"disambiguationData":[TD([[subQ2,1.0]])],"derivedFrom":subQ1}),-1.0]])]});}
            var Q119;
            {var subQ0=sQuery(id+"F0.wireOp",EDGE,"E4.69.0");var subQ1=sQuery(id+"F0.wireOp",EDGE,"E1");var subQ2=makeQuery(id+"F0.imprint","INTERSECT",VERTEX,{"derivedFrom":[subQ1,subQ0]});Q119=makeQuery(id+"F0.imprint","IMPRINT",FACE,{"disambiguationData":[TD([[makeQuery(id+"F0.imprint","IMPRINT",EDGE,{"disambiguationData":[TD([[subQ2,1.0]])],"derivedFrom":subQ1}),-1.0]])]});}
            var Q120;
            {var subQ0=sQuery(id+"F0.wireOp",EDGE,"E4.68.0");var subQ1=sQuery(id+"F0.wireOp",EDGE,"E1");var subQ2=makeQuery(id+"F0.imprint","INTERSECT",VERTEX,{"derivedFrom":[subQ1,subQ0]});Q120=makeQuery(id+"F0.imprint","IMPRINT",FACE,{"disambiguationData":[TD([[makeQuery(id+"F0.imprint","IMPRINT",EDGE,{"disambiguationData":[TD([[subQ2,1.0]])],"derivedFrom":subQ1}),-1.0]])]});}
            var Q121;
            {var subQ0=sQuery(id+"F0.wireOp",EDGE,"E4.67.0");var subQ1=sQuery(id+"F0.wireOp",EDGE,"E1");var subQ2=makeQuery(id+"F0.imprint","INTERSECT",VERTEX,{"derivedFrom":[subQ1,subQ0]});Q121=makeQuery(id+"F0.imprint","IMPRINT",FACE,{"disambiguationData":[TD([[makeQuery(id+"F0.imprint","IMPRINT",EDGE,{"disambiguationData":[TD([[subQ2,1.0]])],"derivedFrom":subQ1}),-1.0]])]});}
            var Q122;
            {var subQ0=sQuery(id+"F0.wireOp",EDGE,"E4.66.0");var subQ1=sQuery(id+"F0.wireOp",EDGE,"E1");var subQ2=makeQuery(id+"F0.imprint","INTERSECT",VERTEX,{"derivedFrom":[subQ1,subQ0]});Q122=makeQuery(id+"F0.imprint","IMPRINT",FACE,{"disambiguationData":[TD([[makeQuery(id+"F0.imprint","IMPRINT",EDGE,{"disambiguationData":[TD([[subQ2,1.0]])],"derivedFrom":subQ1}),-1.0]])]});}
            var Q123;
            {var subQ0=sQuery(id+"F0.wireOp",EDGE,"E4.65.0");var subQ1=sQuery(id+"F0.wireOp",EDGE,"E1");var subQ2=makeQuery(id+"F0.imprint","INTERSECT",VERTEX,{"derivedFrom":[subQ1,subQ0]});Q123=makeQuery(id+"F0.imprint","IMPRINT",FACE,{"disambiguationData":[TD([[makeQuery(id+"F0.imprint","IMPRINT",EDGE,{"disambiguationData":[TD([[subQ2,1.0]])],"derivedFrom":subQ1}),-1.0]])]});}
            var Q124;
            {var subQ0=sQuery(id+"F0.wireOp",EDGE,"E4.64.0");var subQ1=sQuery(id+"F0.wireOp",EDGE,"E1");var subQ2=makeQuery(id+"F0.imprint","INTERSECT",VERTEX,{"derivedFrom":[subQ1,subQ0]});Q124=makeQuery(id+"F0.imprint","IMPRINT",FACE,{"disambiguationData":[TD([[makeQuery(id+"F0.imprint","IMPRINT",EDGE,{"disambiguationData":[TD([[subQ2,1.0]])],"derivedFrom":subQ1}),-1.0]])]});}
            var Q125;
            {var subQ0=sQuery(id+"F0.wireOp",EDGE,"E4.63.0");var subQ1=sQuery(id+"F0.wireOp",EDGE,"E1");var subQ2=makeQuery(id+"F0.imprint","INTERSECT",VERTEX,{"derivedFrom":[subQ1,subQ0]});Q125=makeQuery(id+"F0.imprint","IMPRINT",FACE,{"disambiguationData":[TD([[makeQuery(id+"F0.imprint","IMPRINT",EDGE,{"disambiguationData":[TD([[subQ2,1.0]])],"derivedFrom":subQ1}),-1.0]])]});}
            var Q126;
            {var subQ0=sQuery(id+"F0.wireOp",EDGE,"E4.62.0");var subQ1=sQuery(id+"F0.wireOp",EDGE,"E1");var subQ2=makeQuery(id+"F0.imprint","INTERSECT",VERTEX,{"derivedFrom":[subQ1,subQ0]});Q126=makeQuery(id+"F0.imprint","IMPRINT",FACE,{"disambiguationData":[TD([[makeQuery(id+"F0.imprint","IMPRINT",EDGE,{"disambiguationData":[TD([[subQ2,1.0]])],"derivedFrom":subQ1}),-1.0]])]});}
            var Q127;
            {var subQ0=sQuery(id+"F0.wireOp",EDGE,"E4.61.0");var subQ1=sQuery(id+"F0.wireOp",EDGE,"E1");var subQ2=makeQuery(id+"F0.imprint","INTERSECT",VERTEX,{"derivedFrom":[subQ1,subQ0]});Q127=makeQuery(id+"F0.imprint","IMPRINT",FACE,{"disambiguationData":[TD([[makeQuery(id+"F0.imprint","IMPRINT",EDGE,{"disambiguationData":[TD([[subQ2,1.0]])],"derivedFrom":subQ1}),-1.0]])]});}
            var Q128;
            {var subQ0=sQuery(id+"F0.wireOp",EDGE,"E4.80.0");var subQ1=sQuery(id+"F0.wireOp",EDGE,"E1");var subQ2=makeQuery(id+"F0.imprint","INTERSECT",VERTEX,{"derivedFrom":[subQ1,subQ0]});Q128=makeQuery(id+"F0.imprint","IMPRINT",FACE,{"disambiguationData":[TD([[makeQuery(id+"F0.imprint","IMPRINT",EDGE,{"disambiguationData":[TD([[subQ2,1.0]])],"derivedFrom":subQ1}),-1.0]])]});}
            var Q129;
            {var subQ0=sQuery(id+"F0.wireOp",EDGE,"E4.91.0");var subQ1=sQuery(id+"F0.wireOp",EDGE,"E1");var subQ2=makeQuery(id+"F0.imprint","INTERSECT",VERTEX,{"derivedFrom":[subQ1,subQ0]});Q129=makeQuery(id+"F0.imprint","IMPRINT",FACE,{"disambiguationData":[TD([[makeQuery(id+"F0.imprint","IMPRINT",EDGE,{"disambiguationData":[TD([[subQ2,1.0]])],"derivedFrom":subQ1}),-1.0]])]});}
            var Q130;
            {var subQ0=sQuery(id+"F0.wireOp",EDGE,"E4.81.0");var subQ1=sQuery(id+"F0.wireOp",EDGE,"E1");var subQ2=makeQuery(id+"F0.imprint","INTERSECT",VERTEX,{"derivedFrom":[subQ1,subQ0]});Q130=makeQuery(id+"F0.imprint","IMPRINT",FACE,{"disambiguationData":[TD([[makeQuery(id+"F0.imprint","IMPRINT",EDGE,{"disambiguationData":[TD([[subQ2,1.0]])],"derivedFrom":subQ1}),-1.0]])]});}
            var Q131;
            {var subQ0=sQuery(id+"F0.wireOp",EDGE,"E4.92.0");var subQ1=sQuery(id+"F0.wireOp",EDGE,"E1");var subQ2=makeQuery(id+"F0.imprint","INTERSECT",VERTEX,{"derivedFrom":[subQ1,subQ0]});Q131=makeQuery(id+"F0.imprint","IMPRINT",FACE,{"disambiguationData":[TD([[makeQuery(id+"F0.imprint","IMPRINT",EDGE,{"disambiguationData":[TD([[subQ2,1.0]])],"derivedFrom":subQ1}),-1.0]])]});}
            var Q132;
            {var subQ0=sQuery(id+"F0.wireOp",EDGE,"E4.82.0");var subQ1=sQuery(id+"F0.wireOp",EDGE,"E1");var subQ2=makeQuery(id+"F0.imprint","INTERSECT",VERTEX,{"derivedFrom":[subQ1,subQ0]});Q132=makeQuery(id+"F0.imprint","IMPRINT",FACE,{"disambiguationData":[TD([[makeQuery(id+"F0.imprint","IMPRINT",EDGE,{"disambiguationData":[TD([[subQ2,1.0]])],"derivedFrom":subQ1}),-1.0]])]});}
            var Q133;
            {var subQ0=sQuery(id+"F0.wireOp",EDGE,"E4.93.0");var subQ1=sQuery(id+"F0.wireOp",EDGE,"E1");var subQ2=makeQuery(id+"F0.imprint","INTERSECT",VERTEX,{"derivedFrom":[subQ1,subQ0]});Q133=makeQuery(id+"F0.imprint","IMPRINT",FACE,{"disambiguationData":[TD([[makeQuery(id+"F0.imprint","IMPRINT",EDGE,{"disambiguationData":[TD([[subQ2,1.0]])],"derivedFrom":subQ1}),-1.0]])]});}
            var Q134;
            {var subQ0=sQuery(id+"F0.wireOp",EDGE,"E4.94.0");var subQ1=sQuery(id+"F0.wireOp",EDGE,"E1");var subQ2=makeQuery(id+"F0.imprint","INTERSECT",VERTEX,{"derivedFrom":[subQ1,subQ0]});Q134=makeQuery(id+"F0.imprint","IMPRINT",FACE,{"disambiguationData":[TD([[makeQuery(id+"F0.imprint","IMPRINT",EDGE,{"disambiguationData":[TD([[subQ2,1.0]])],"derivedFrom":subQ1}),-1.0]])]});}
            var Q135;
            {var subQ0=sQuery(id+"F0.wireOp",EDGE,"E4.95.0");var subQ1=sQuery(id+"F0.wireOp",EDGE,"E1");var subQ2=makeQuery(id+"F0.imprint","INTERSECT",VERTEX,{"derivedFrom":[subQ1,subQ0]});Q135=makeQuery(id+"F0.imprint","IMPRINT",FACE,{"disambiguationData":[TD([[makeQuery(id+"F0.imprint","IMPRINT",EDGE,{"disambiguationData":[TD([[subQ2,1.0]])],"derivedFrom":subQ1}),-1.0]])]});}
            var Q136;
            {var subQ0=sQuery(id+"F0.wireOp",EDGE,"E4.96.0");var subQ1=sQuery(id+"F0.wireOp",EDGE,"E1");var subQ2=makeQuery(id+"F0.imprint","INTERSECT",VERTEX,{"derivedFrom":[subQ1,subQ0]});Q136=makeQuery(id+"F0.imprint","IMPRINT",FACE,{"disambiguationData":[TD([[makeQuery(id+"F0.imprint","IMPRINT",EDGE,{"disambiguationData":[TD([[subQ2,1.0]])],"derivedFrom":subQ1}),-1.0]])]});}
            var Q137;
            {var subQ0=sQuery(id+"F0.wireOp",EDGE,"E4.97.0");var subQ1=sQuery(id+"F0.wireOp",EDGE,"E1");var subQ2=makeQuery(id+"F0.imprint","INTERSECT",VERTEX,{"derivedFrom":[subQ1,subQ0]});Q137=makeQuery(id+"F0.imprint","IMPRINT",FACE,{"disambiguationData":[TD([[makeQuery(id+"F0.imprint","IMPRINT",EDGE,{"disambiguationData":[TD([[subQ2,1.0]])],"derivedFrom":subQ1}),-1.0]])]});}
            var Q138;
            {var subQ0=sQuery(id+"F0.wireOp",EDGE,"E4.98.0");var subQ1=sQuery(id+"F0.wireOp",EDGE,"E1");var subQ2=makeQuery(id+"F0.imprint","INTERSECT",VERTEX,{"derivedFrom":[subQ1,subQ0]});Q138=makeQuery(id+"F0.imprint","IMPRINT",FACE,{"disambiguationData":[TD([[makeQuery(id+"F0.imprint","IMPRINT",EDGE,{"disambiguationData":[TD([[subQ2,1.0]])],"derivedFrom":subQ1}),-1.0]])]});}
            var Q139;
            {var subQ0=sQuery(id+"F0.wireOp",EDGE,"E4.99.0");var subQ1=sQuery(id+"F0.wireOp",EDGE,"E1");var subQ2=makeQuery(id+"F0.imprint","INTERSECT",VERTEX,{"derivedFrom":[subQ1,subQ0]});Q139=makeQuery(id+"F0.imprint","IMPRINT",FACE,{"disambiguationData":[TD([[makeQuery(id+"F0.imprint","IMPRINT",EDGE,{"disambiguationData":[TD([[subQ2,1.0]])],"derivedFrom":subQ1}),-1.0]])]});}
            var Q140;
            {var subQ0=sQuery(id+"F0.wireOp",EDGE,"E4.101.0");var subQ1=sQuery(id+"F0.wireOp",EDGE,"E1");var subQ2=makeQuery(id+"F0.imprint","INTERSECT",VERTEX,{"derivedFrom":[subQ1,subQ0]});Q140=makeQuery(id+"F0.imprint","IMPRINT",FACE,{"disambiguationData":[TD([[makeQuery(id+"F0.imprint","IMPRINT",EDGE,{"disambiguationData":[TD([[subQ2,1.0]])],"derivedFrom":subQ1}),-1.0]])]});}
            var Q141;
            {var subQ0=sQuery(id+"F0.wireOp",EDGE,"E4.102.0");var subQ1=sQuery(id+"F0.wireOp",EDGE,"E1");var subQ2=makeQuery(id+"F0.imprint","INTERSECT",VERTEX,{"derivedFrom":[subQ1,subQ0]});Q141=makeQuery(id+"F0.imprint","IMPRINT",FACE,{"disambiguationData":[TD([[makeQuery(id+"F0.imprint","IMPRINT",EDGE,{"disambiguationData":[TD([[subQ2,1.0]])],"derivedFrom":subQ1}),-1.0]])]});}
            var Q142;
            {var subQ0=sQuery(id+"F0.wireOp",EDGE,"E4.103.0");var subQ1=sQuery(id+"F0.wireOp",EDGE,"E1");var subQ2=makeQuery(id+"F0.imprint","INTERSECT",VERTEX,{"derivedFrom":[subQ1,subQ0]});Q142=makeQuery(id+"F0.imprint","IMPRINT",FACE,{"disambiguationData":[TD([[makeQuery(id+"F0.imprint","IMPRINT",EDGE,{"disambiguationData":[TD([[subQ2,1.0]])],"derivedFrom":subQ1}),-1.0]])]});}
            var Q143;
            {var subQ0=sQuery(id+"F0.wireOp",EDGE,"E4.104.0");var subQ1=sQuery(id+"F0.wireOp",EDGE,"E1");var subQ2=makeQuery(id+"F0.imprint","INTERSECT",VERTEX,{"derivedFrom":[subQ1,subQ0]});Q143=makeQuery(id+"F0.imprint","IMPRINT",FACE,{"disambiguationData":[TD([[makeQuery(id+"F0.imprint","IMPRINT",EDGE,{"disambiguationData":[TD([[subQ2,1.0]])],"derivedFrom":subQ1}),-1.0]])]});}
            var Q144;
            {var subQ0=sQuery(id+"F0.wireOp",EDGE,"E4.105.0");var subQ1=sQuery(id+"F0.wireOp",EDGE,"E1");var subQ2=makeQuery(id+"F0.imprint","INTERSECT",VERTEX,{"derivedFrom":[subQ1,subQ0]});Q144=makeQuery(id+"F0.imprint","IMPRINT",FACE,{"disambiguationData":[TD([[makeQuery(id+"F0.imprint","IMPRINT",EDGE,{"disambiguationData":[TD([[subQ2,1.0]])],"derivedFrom":subQ1}),-1.0]])]});}
            var Q145;
            {var subQ0=sQuery(id+"F0.wireOp",EDGE,"E4.106.0");var subQ1=sQuery(id+"F0.wireOp",EDGE,"E1");var subQ2=makeQuery(id+"F0.imprint","INTERSECT",VERTEX,{"derivedFrom":[subQ1,subQ0]});Q145=makeQuery(id+"F0.imprint","IMPRINT",FACE,{"disambiguationData":[TD([[makeQuery(id+"F0.imprint","IMPRINT",EDGE,{"disambiguationData":[TD([[subQ2,1.0]])],"derivedFrom":subQ1}),-1.0]])]});}
            var Q146;
            {var subQ0=sQuery(id+"F0.wireOp",EDGE,"E4.107.0");var subQ1=sQuery(id+"F0.wireOp",EDGE,"E1");var subQ2=makeQuery(id+"F0.imprint","INTERSECT",VERTEX,{"derivedFrom":[subQ1,subQ0]});Q146=makeQuery(id+"F0.imprint","IMPRINT",FACE,{"disambiguationData":[TD([[makeQuery(id+"F0.imprint","IMPRINT",EDGE,{"disambiguationData":[TD([[subQ2,1.0]])],"derivedFrom":subQ1}),-1.0]])]});}
            var Q147;
            {var subQ0=sQuery(id+"F0.wireOp",EDGE,"E4.108.0");var subQ1=sQuery(id+"F0.wireOp",EDGE,"E1");var subQ2=makeQuery(id+"F0.imprint","INTERSECT",VERTEX,{"derivedFrom":[subQ1,subQ0]});Q147=makeQuery(id+"F0.imprint","IMPRINT",FACE,{"disambiguationData":[TD([[makeQuery(id+"F0.imprint","IMPRINT",EDGE,{"disambiguationData":[TD([[subQ2,1.0]])],"derivedFrom":subQ1}),-1.0]])]});}
            var Q148;
            {var subQ0=sQuery(id+"F0.wireOp",EDGE,"E3");var subQ1=sQuery(id+"F0.wireOp",EDGE,"E1");var subQ2=makeQuery(id+"F0.imprint","INTERSECT",VERTEX,{"derivedFrom":[subQ1,subQ0]});Q148=makeQuery(id+"F0.imprint","IMPRINT",FACE,{"disambiguationData":[TD([[makeQuery(id+"F0.imprint","IMPRINT",EDGE,{"disambiguationData":[TD([[subQ2,-1.0]])],"derivedFrom":subQ1}),-1.0]])]});}
            var Q149;
            {var subQ0=sQuery(id+"F0.wireOp",EDGE,"E2");var subQ1=sQuery(id+"F0.wireOp",EDGE,"E1");var subQ2=makeQuery(id+"F0.imprint","INTERSECT",VERTEX,{"derivedFrom":[subQ1,subQ0]});Q149=makeQuery(id+"F0.imprint","IMPRINT",FACE,{"disambiguationData":[TD([[makeQuery(id+"F0.imprint","IMPRINT",EDGE,{"disambiguationData":[TD([[subQ2,1.0]])],"derivedFrom":subQ1}),-1.0]])]});}
            var Q150;
            {var subQ0=sQuery(id+"F0.wireOp",EDGE,"E4.1.0");var subQ1=sQuery(id+"F0.wireOp",EDGE,"E1");var subQ2=makeQuery(id+"F0.imprint","INTERSECT",VERTEX,{"derivedFrom":[subQ1,subQ0]});Q150=makeQuery(id+"F0.imprint","IMPRINT",FACE,{"disambiguationData":[TD([[makeQuery(id+"F0.imprint","IMPRINT",EDGE,{"disambiguationData":[TD([[subQ2,1.0]])],"derivedFrom":subQ1}),-1.0]])]});}
            var Q151;
            {var subQ0=sQuery(id+"F0.wireOp",EDGE,"E4.2.0");var subQ1=sQuery(id+"F0.wireOp",EDGE,"E1");var subQ2=makeQuery(id+"F0.imprint","INTERSECT",VERTEX,{"derivedFrom":[subQ1,subQ0]});Q151=makeQuery(id+"F0.imprint","IMPRINT",FACE,{"disambiguationData":[TD([[makeQuery(id+"F0.imprint","IMPRINT",EDGE,{"disambiguationData":[TD([[subQ2,1.0]])],"derivedFrom":subQ1}),-1.0]])]});}
            var Q152;
            {var subQ0=sQuery(id+"F0.wireOp",EDGE,"E4.3.0");var subQ1=sQuery(id+"F0.wireOp",EDGE,"E1");var subQ2=makeQuery(id+"F0.imprint","INTERSECT",VERTEX,{"derivedFrom":[subQ1,subQ0]});Q152=makeQuery(id+"F0.imprint","IMPRINT",FACE,{"disambiguationData":[TD([[makeQuery(id+"F0.imprint","IMPRINT",EDGE,{"disambiguationData":[TD([[subQ2,1.0]])],"derivedFrom":subQ1}),-1.0]])]});}
            var Q153;
            {var subQ0=sQuery(id+"F0.wireOp",EDGE,"E4.4.0");var subQ1=sQuery(id+"F0.wireOp",EDGE,"E1");var subQ2=makeQuery(id+"F0.imprint","INTERSECT",VERTEX,{"derivedFrom":[subQ1,subQ0]});Q153=makeQuery(id+"F0.imprint","IMPRINT",FACE,{"disambiguationData":[TD([[makeQuery(id+"F0.imprint","IMPRINT",EDGE,{"disambiguationData":[TD([[subQ2,1.0]])],"derivedFrom":subQ1}),-1.0]])]});}
            var Q154;
            {var subQ0=sQuery(id+"F0.wireOp",EDGE,"E4.5.0");var subQ1=sQuery(id+"F0.wireOp",EDGE,"E1");var subQ2=makeQuery(id+"F0.imprint","INTERSECT",VERTEX,{"derivedFrom":[subQ1,subQ0]});Q154=makeQuery(id+"F0.imprint","IMPRINT",FACE,{"disambiguationData":[TD([[makeQuery(id+"F0.imprint","IMPRINT",EDGE,{"disambiguationData":[TD([[subQ2,1.0]])],"derivedFrom":subQ1}),-1.0]])]});}
            var Q155;
            {var subQ0=sQuery(id+"F0.wireOp",EDGE,"E4.18.0");var subQ1=sQuery(id+"F0.wireOp",EDGE,"E1");var subQ2=makeQuery(id+"F0.imprint","INTERSECT",VERTEX,{"derivedFrom":[subQ1,subQ0]});Q155=makeQuery(id+"F0.imprint","IMPRINT",FACE,{"disambiguationData":[TD([[makeQuery(id+"F0.imprint","IMPRINT",EDGE,{"disambiguationData":[TD([[subQ2,1.0]])],"derivedFrom":subQ1}),-1.0]])]});}
            var Q156;
            {var subQ0=sQuery(id+"F0.wireOp",EDGE,"E4.19.0");var subQ1=sQuery(id+"F0.wireOp",EDGE,"E1");var subQ2=makeQuery(id+"F0.imprint","INTERSECT",VERTEX,{"derivedFrom":[subQ1,subQ0]});Q156=makeQuery(id+"F0.imprint","IMPRINT",FACE,{"disambiguationData":[TD([[makeQuery(id+"F0.imprint","IMPRINT",EDGE,{"disambiguationData":[TD([[subQ2,1.0]])],"derivedFrom":subQ1}),-1.0]])]});}
            var Q157;
            {var subQ0=sQuery(id+"F0.wireOp",EDGE,"E4.21.0");var subQ1=sQuery(id+"F0.wireOp",EDGE,"E1");var subQ2=makeQuery(id+"F0.imprint","INTERSECT",VERTEX,{"derivedFrom":[subQ1,subQ0]});Q157=makeQuery(id+"F0.imprint","IMPRINT",FACE,{"disambiguationData":[TD([[makeQuery(id+"F0.imprint","IMPRINT",EDGE,{"disambiguationData":[TD([[subQ2,1.0]])],"derivedFrom":subQ1}),-1.0]])]});}
            var Q158;
            {var subQ0=sQuery(id+"F0.wireOp",EDGE,"E4.22.0");var subQ1=sQuery(id+"F0.wireOp",EDGE,"E1");var subQ2=makeQuery(id+"F0.imprint","INTERSECT",VERTEX,{"derivedFrom":[subQ1,subQ0]});Q158=makeQuery(id+"F0.imprint","IMPRINT",FACE,{"disambiguationData":[TD([[makeQuery(id+"F0.imprint","IMPRINT",EDGE,{"disambiguationData":[TD([[subQ2,1.0]])],"derivedFrom":subQ1}),-1.0]])]});}
            var Q159;
            {var subQ0=sQuery(id+"F0.wireOp",EDGE,"E4.23.0");var subQ1=sQuery(id+"F0.wireOp",EDGE,"E1");var subQ2=makeQuery(id+"F0.imprint","INTERSECT",VERTEX,{"derivedFrom":[subQ1,subQ0]});Q159=makeQuery(id+"F0.imprint","IMPRINT",FACE,{"disambiguationData":[TD([[makeQuery(id+"F0.imprint","IMPRINT",EDGE,{"disambiguationData":[TD([[subQ2,1.0]])],"derivedFrom":subQ1}),-1.0]])]});}
            var Q160;
            {var subQ0=sQuery(id+"F0.wireOp",EDGE,"E4.27.0");var subQ1=sQuery(id+"F0.wireOp",EDGE,"E1");var subQ2=makeQuery(id+"F0.imprint","INTERSECT",VERTEX,{"derivedFrom":[subQ1,subQ0]});Q160=makeQuery(id+"F0.imprint","IMPRINT",FACE,{"disambiguationData":[TD([[makeQuery(id+"F0.imprint","IMPRINT",EDGE,{"disambiguationData":[TD([[subQ2,1.0]])],"derivedFrom":subQ1}),-1.0]])]});}
            var Q161;
            {var subQ0=sQuery(id+"F0.wireOp",EDGE,"E4.28.0");var subQ1=sQuery(id+"F0.wireOp",EDGE,"E1");var subQ2=makeQuery(id+"F0.imprint","INTERSECT",VERTEX,{"derivedFrom":[subQ1,subQ0]});Q161=makeQuery(id+"F0.imprint","IMPRINT",FACE,{"disambiguationData":[TD([[makeQuery(id+"F0.imprint","IMPRINT",EDGE,{"disambiguationData":[TD([[subQ2,1.0]])],"derivedFrom":subQ1}),-1.0]])]});}
            var Q162;
            {var subQ0=sQuery(id+"F0.wireOp",EDGE,"E4.26.0");var subQ1=sQuery(id+"F0.wireOp",EDGE,"E1");var subQ2=makeQuery(id+"F0.imprint","INTERSECT",VERTEX,{"derivedFrom":[subQ1,subQ0]});Q162=makeQuery(id+"F0.imprint","IMPRINT",FACE,{"disambiguationData":[TD([[makeQuery(id+"F0.imprint","IMPRINT",EDGE,{"disambiguationData":[TD([[subQ2,1.0]])],"derivedFrom":subQ1}),-1.0]])]});}
            var Q163;
            {var subQ0=sQuery(id+"F0.wireOp",EDGE,"E4.25.0");var subQ1=sQuery(id+"F0.wireOp",EDGE,"E1");var subQ2=makeQuery(id+"F0.imprint","INTERSECT",VERTEX,{"derivedFrom":[subQ1,subQ0]});Q163=makeQuery(id+"F0.imprint","IMPRINT",FACE,{"disambiguationData":[TD([[makeQuery(id+"F0.imprint","IMPRINT",EDGE,{"disambiguationData":[TD([[subQ2,1.0]])],"derivedFrom":subQ1}),-1.0]])]});}
            var Q164;
            {var subQ0=sQuery(id+"F0.wireOp",EDGE,"E4.24.0");var subQ1=sQuery(id+"F0.wireOp",EDGE,"E1");var subQ2=makeQuery(id+"F0.imprint","INTERSECT",VERTEX,{"derivedFrom":[subQ1,subQ0]});Q164=makeQuery(id+"F0.imprint","IMPRINT",FACE,{"disambiguationData":[TD([[makeQuery(id+"F0.imprint","IMPRINT",EDGE,{"disambiguationData":[TD([[subQ2,1.0]])],"derivedFrom":subQ1}),-1.0]])]});}
            var Q165;
            {var subQ0=sQuery(id+"F0.wireOp",EDGE,"E4.17.0");var subQ1=sQuery(id+"F0.wireOp",EDGE,"E1");var subQ2=makeQuery(id+"F0.imprint","INTERSECT",VERTEX,{"derivedFrom":[subQ1,subQ0]});Q165=makeQuery(id+"F0.imprint","IMPRINT",FACE,{"disambiguationData":[TD([[makeQuery(id+"F0.imprint","IMPRINT",EDGE,{"disambiguationData":[TD([[subQ2,1.0]])],"derivedFrom":subQ1}),-1.0]])]});}
            var Q166;
            {var subQ0=sQuery(id+"F0.wireOp",EDGE,"E4.16.0");var subQ1=sQuery(id+"F0.wireOp",EDGE,"E1");var subQ2=makeQuery(id+"F0.imprint","INTERSECT",VERTEX,{"derivedFrom":[subQ1,subQ0]});Q166=makeQuery(id+"F0.imprint","IMPRINT",FACE,{"disambiguationData":[TD([[makeQuery(id+"F0.imprint","IMPRINT",EDGE,{"disambiguationData":[TD([[subQ2,1.0]])],"derivedFrom":subQ1}),-1.0]])]});}
            var Q167;
            {var subQ0=sQuery(id+"F0.wireOp",EDGE,"E4.15.0");var subQ1=sQuery(id+"F0.wireOp",EDGE,"E1");var subQ2=makeQuery(id+"F0.imprint","INTERSECT",VERTEX,{"derivedFrom":[subQ1,subQ0]});Q167=makeQuery(id+"F0.imprint","IMPRINT",FACE,{"disambiguationData":[TD([[makeQuery(id+"F0.imprint","IMPRINT",EDGE,{"disambiguationData":[TD([[subQ2,1.0]])],"derivedFrom":subQ1}),-1.0]])]});}
            var Q168;
            {var subQ0=sQuery(id+"F0.wireOp",EDGE,"E4.14.0");var subQ1=sQuery(id+"F0.wireOp",EDGE,"E1");var subQ2=makeQuery(id+"F0.imprint","INTERSECT",VERTEX,{"derivedFrom":[subQ1,subQ0]});Q168=makeQuery(id+"F0.imprint","IMPRINT",FACE,{"disambiguationData":[TD([[makeQuery(id+"F0.imprint","IMPRINT",EDGE,{"disambiguationData":[TD([[subQ2,1.0]])],"derivedFrom":subQ1}),-1.0]])]});}
            var Q169;
            {var subQ0=sQuery(id+"F0.wireOp",EDGE,"E4.12.0");var subQ1=sQuery(id+"F0.wireOp",EDGE,"E1");var subQ2=makeQuery(id+"F0.imprint","INTERSECT",VERTEX,{"derivedFrom":[subQ1,subQ0]});Q169=makeQuery(id+"F0.imprint","IMPRINT",FACE,{"disambiguationData":[TD([[makeQuery(id+"F0.imprint","IMPRINT",EDGE,{"disambiguationData":[TD([[subQ2,1.0]])],"derivedFrom":subQ1}),-1.0]])]});}
            var Q170;
            {var subQ0=sQuery(id+"F0.wireOp",EDGE,"E4.11.0");var subQ1=sQuery(id+"F0.wireOp",EDGE,"E1");var subQ2=makeQuery(id+"F0.imprint","INTERSECT",VERTEX,{"derivedFrom":[subQ1,subQ0]});Q170=makeQuery(id+"F0.imprint","IMPRINT",FACE,{"disambiguationData":[TD([[makeQuery(id+"F0.imprint","IMPRINT",EDGE,{"disambiguationData":[TD([[subQ2,1.0]])],"derivedFrom":subQ1}),-1.0]])]});}
            var Q171;
            {var subQ0=sQuery(id+"F0.wireOp",EDGE,"E4.10.0");var subQ1=sQuery(id+"F0.wireOp",EDGE,"E1");var subQ2=makeQuery(id+"F0.imprint","INTERSECT",VERTEX,{"derivedFrom":[subQ1,subQ0]});Q171=makeQuery(id+"F0.imprint","IMPRINT",FACE,{"disambiguationData":[TD([[makeQuery(id+"F0.imprint","IMPRINT",EDGE,{"disambiguationData":[TD([[subQ2,1.0]])],"derivedFrom":subQ1}),-1.0]])]});}
            var Q172;
            {var subQ0=sQuery(id+"F0.wireOp",EDGE,"E4.9.0");var subQ1=sQuery(id+"F0.wireOp",EDGE,"E1");var subQ2=makeQuery(id+"F0.imprint","INTERSECT",VERTEX,{"derivedFrom":[subQ1,subQ0]});Q172=makeQuery(id+"F0.imprint","IMPRINT",FACE,{"disambiguationData":[TD([[makeQuery(id+"F0.imprint","IMPRINT",EDGE,{"disambiguationData":[TD([[subQ2,1.0]])],"derivedFrom":subQ1}),-1.0]])]});}
            var Q173;
            {var subQ0=sQuery(id+"F0.wireOp",EDGE,"E4.8.0");var subQ1=sQuery(id+"F0.wireOp",EDGE,"E1");var subQ2=makeQuery(id+"F0.imprint","INTERSECT",VERTEX,{"derivedFrom":[subQ1,subQ0]});Q173=makeQuery(id+"F0.imprint","IMPRINT",FACE,{"disambiguationData":[TD([[makeQuery(id+"F0.imprint","IMPRINT",EDGE,{"disambiguationData":[TD([[subQ2,1.0]])],"derivedFrom":subQ1}),-1.0]])]});}
            var Q174;
            {var subQ0=sQuery(id+"F0.wireOp",EDGE,"E4.7.0");var subQ1=sQuery(id+"F0.wireOp",EDGE,"E1");var subQ2=makeQuery(id+"F0.imprint","INTERSECT",VERTEX,{"derivedFrom":[subQ1,subQ0]});Q174=makeQuery(id+"F0.imprint","IMPRINT",FACE,{"disambiguationData":[TD([[makeQuery(id+"F0.imprint","IMPRINT",EDGE,{"disambiguationData":[TD([[subQ2,1.0]])],"derivedFrom":subQ1}),-1.0]])]});}
            var Q175;
            {var subQ0=sQuery(id+"F0.wireOp",EDGE,"E4.6.0");var subQ1=sQuery(id+"F0.wireOp",EDGE,"E1");var subQ2=makeQuery(id+"F0.imprint","INTERSECT",VERTEX,{"derivedFrom":[subQ1,subQ0]});Q175=makeQuery(id+"F0.imprint","IMPRINT",FACE,{"disambiguationData":[TD([[makeQuery(id+"F0.imprint","IMPRINT",EDGE,{"disambiguationData":[TD([[subQ2,1.0]])],"derivedFrom":subQ1}),-1.0]])]});}
            var Q176;
            {var subQ0=sQuery(id+"F0.wireOp",EDGE,"E4.90.0");var subQ1=sQuery(id+"F0.wireOp",EDGE,"E1");var subQ2=makeQuery(id+"F0.imprint","INTERSECT",VERTEX,{"derivedFrom":[subQ1,subQ0]});Q176=makeQuery(id+"F0.imprint","IMPRINT",FACE,{"disambiguationData":[TD([[makeQuery(id+"F0.imprint","IMPRINT",EDGE,{"disambiguationData":[TD([[subQ2,1.0]])],"derivedFrom":subQ1}),-1.0]])]});}
            var Q177;
            {var subQ0=sQuery(id+"F0.wireOp",EDGE,"E4.79.0");var subQ1=sQuery(id+"F0.wireOp",EDGE,"E1");var subQ2=makeQuery(id+"F0.imprint","INTERSECT",VERTEX,{"derivedFrom":[subQ1,subQ0]});Q177=makeQuery(id+"F0.imprint","IMPRINT",FACE,{"disambiguationData":[TD([[makeQuery(id+"F0.imprint","IMPRINT",EDGE,{"disambiguationData":[TD([[subQ2,1.0]])],"derivedFrom":subQ1}),-1.0]])]});}
            var Q178;
            {var subQ0=sQuery(id+"F0.wireOp",EDGE,"E4.89.0");var subQ1=sQuery(id+"F0.wireOp",EDGE,"E1");var subQ2=makeQuery(id+"F0.imprint","INTERSECT",VERTEX,{"derivedFrom":[subQ1,subQ0]});Q178=makeQuery(id+"F0.imprint","IMPRINT",FACE,{"disambiguationData":[TD([[makeQuery(id+"F0.imprint","IMPRINT",EDGE,{"disambiguationData":[TD([[subQ2,1.0]])],"derivedFrom":subQ1}),-1.0]])]});}
            var Q179;
            {var subQ0=sQuery(id+"F0.wireOp",EDGE,"E4.78.0");var subQ1=sQuery(id+"F0.wireOp",EDGE,"E1");var subQ2=makeQuery(id+"F0.imprint","INTERSECT",VERTEX,{"derivedFrom":[subQ1,subQ0]});Q179=makeQuery(id+"F0.imprint","IMPRINT",FACE,{"disambiguationData":[TD([[makeQuery(id+"F0.imprint","IMPRINT",EDGE,{"disambiguationData":[TD([[subQ2,1.0]])],"derivedFrom":subQ1}),-1.0]])]});}
            var Q180;
            {var subQ0=sQuery(id+"F0.wireOp",EDGE,"E4.88.0");var subQ1=sQuery(id+"F0.wireOp",EDGE,"E1");var subQ2=makeQuery(id+"F0.imprint","INTERSECT",VERTEX,{"derivedFrom":[subQ1,subQ0]});Q180=makeQuery(id+"F0.imprint","IMPRINT",FACE,{"disambiguationData":[TD([[makeQuery(id+"F0.imprint","IMPRINT",EDGE,{"disambiguationData":[TD([[subQ2,1.0]])],"derivedFrom":subQ1}),-1.0]])]});}
            var Q181;
            {var subQ0=sQuery(id+"F0.wireOp",EDGE,"E4.87.0");var subQ1=sQuery(id+"F0.wireOp",EDGE,"E1");var subQ2=makeQuery(id+"F0.imprint","INTERSECT",VERTEX,{"derivedFrom":[subQ1,subQ0]});Q181=makeQuery(id+"F0.imprint","IMPRINT",FACE,{"disambiguationData":[TD([[makeQuery(id+"F0.imprint","IMPRINT",EDGE,{"disambiguationData":[TD([[subQ2,1.0]])],"derivedFrom":subQ1}),-1.0]])]});}
            var Q182;
            {var subQ0=sQuery(id+"F0.wireOp",EDGE,"E4.76.0");var subQ1=sQuery(id+"F0.wireOp",EDGE,"E1");var subQ2=makeQuery(id+"F0.imprint","INTERSECT",VERTEX,{"derivedFrom":[subQ1,subQ0]});Q182=makeQuery(id+"F0.imprint","IMPRINT",FACE,{"disambiguationData":[TD([[makeQuery(id+"F0.imprint","IMPRINT",EDGE,{"disambiguationData":[TD([[subQ2,1.0]])],"derivedFrom":subQ1}),-1.0]])]});}
            var Q183;
            {var subQ0=sQuery(id+"F0.wireOp",EDGE,"E4.86.0");var subQ1=sQuery(id+"F0.wireOp",EDGE,"E1");var subQ2=makeQuery(id+"F0.imprint","INTERSECT",VERTEX,{"derivedFrom":[subQ1,subQ0]});Q183=makeQuery(id+"F0.imprint","IMPRINT",FACE,{"disambiguationData":[TD([[makeQuery(id+"F0.imprint","IMPRINT",EDGE,{"disambiguationData":[TD([[subQ2,1.0]])],"derivedFrom":subQ1}),-1.0]])]});}
            var Q184;
            {var subQ0=sQuery(id+"F0.wireOp",EDGE,"E4.75.0");var subQ1=sQuery(id+"F0.wireOp",EDGE,"E1");var subQ2=makeQuery(id+"F0.imprint","INTERSECT",VERTEX,{"derivedFrom":[subQ1,subQ0]});Q184=makeQuery(id+"F0.imprint","IMPRINT",FACE,{"disambiguationData":[TD([[makeQuery(id+"F0.imprint","IMPRINT",EDGE,{"disambiguationData":[TD([[subQ2,1.0]])],"derivedFrom":subQ1}),-1.0]])]});}
            var Q185;
            {var subQ0=sQuery(id+"F0.wireOp",EDGE,"E4.85.0");var subQ1=sQuery(id+"F0.wireOp",EDGE,"E1");var subQ2=makeQuery(id+"F0.imprint","INTERSECT",VERTEX,{"derivedFrom":[subQ1,subQ0]});Q185=makeQuery(id+"F0.imprint","IMPRINT",FACE,{"disambiguationData":[TD([[makeQuery(id+"F0.imprint","IMPRINT",EDGE,{"disambiguationData":[TD([[subQ2,1.0]])],"derivedFrom":subQ1}),-1.0]])]});}
            var Q186;
            {var subQ0=sQuery(id+"F0.wireOp",EDGE,"E4.74.0");var subQ1=sQuery(id+"F0.wireOp",EDGE,"E1");var subQ2=makeQuery(id+"F0.imprint","INTERSECT",VERTEX,{"derivedFrom":[subQ1,subQ0]});Q186=makeQuery(id+"F0.imprint","IMPRINT",FACE,{"disambiguationData":[TD([[makeQuery(id+"F0.imprint","IMPRINT",EDGE,{"disambiguationData":[TD([[subQ2,1.0]])],"derivedFrom":subQ1}),-1.0]])]});}
            var Q187;
            {var subQ0=sQuery(id+"F0.wireOp",EDGE,"E4.84.0");var subQ1=sQuery(id+"F0.wireOp",EDGE,"E1");var subQ2=makeQuery(id+"F0.imprint","INTERSECT",VERTEX,{"derivedFrom":[subQ1,subQ0]});Q187=makeQuery(id+"F0.imprint","IMPRINT",FACE,{"disambiguationData":[TD([[makeQuery(id+"F0.imprint","IMPRINT",EDGE,{"disambiguationData":[TD([[subQ2,1.0]])],"derivedFrom":subQ1}),-1.0]])]});}
            var Q188;
            {var subQ0=sQuery(id+"F0.wireOp",EDGE,"E4.40.0");var subQ1=sQuery(id+"F0.wireOp",EDGE,"E1");var subQ2=makeQuery(id+"F0.imprint","INTERSECT",VERTEX,{"derivedFrom":[subQ1,subQ0]});Q188=makeQuery(id+"F0.imprint","IMPRINT",FACE,{"disambiguationData":[TD([[makeQuery(id+"F0.imprint","IMPRINT",EDGE,{"disambiguationData":[TD([[subQ2,1.0]])],"derivedFrom":subQ1}),-1.0]])]});}
            var Q189;
            {var subQ0=sQuery(id+"F0.wireOp",EDGE,"E4.39.0");var subQ1=sQuery(id+"F0.wireOp",EDGE,"E1");var subQ2=makeQuery(id+"F0.imprint","INTERSECT",VERTEX,{"derivedFrom":[subQ1,subQ0]});Q189=makeQuery(id+"F0.imprint","IMPRINT",FACE,{"disambiguationData":[TD([[makeQuery(id+"F0.imprint","IMPRINT",EDGE,{"disambiguationData":[TD([[subQ2,1.0]])],"derivedFrom":subQ1}),-1.0]])]});}
            var Q190;
            {var subQ0=sQuery(id+"F0.wireOp",EDGE,"E4.38.0");var subQ1=sQuery(id+"F0.wireOp",EDGE,"E1");var subQ2=makeQuery(id+"F0.imprint","INTERSECT",VERTEX,{"derivedFrom":[subQ1,subQ0]});Q190=makeQuery(id+"F0.imprint","IMPRINT",FACE,{"disambiguationData":[TD([[makeQuery(id+"F0.imprint","IMPRINT",EDGE,{"disambiguationData":[TD([[subQ2,1.0]])],"derivedFrom":subQ1}),-1.0]])]});}
            var Q191;
            {var subQ0=sQuery(id+"F0.wireOp",EDGE,"E4.37.0");var subQ1=sQuery(id+"F0.wireOp",EDGE,"E1");var subQ2=makeQuery(id+"F0.imprint","INTERSECT",VERTEX,{"derivedFrom":[subQ1,subQ0]});Q191=makeQuery(id+"F0.imprint","IMPRINT",FACE,{"disambiguationData":[TD([[makeQuery(id+"F0.imprint","IMPRINT",EDGE,{"disambiguationData":[TD([[subQ2,1.0]])],"derivedFrom":subQ1}),-1.0]])]});}
            var Q192;
            {var subQ0=sQuery(id+"F0.wireOp",EDGE,"E4.36.0");var subQ1=sQuery(id+"F0.wireOp",EDGE,"E1");var subQ2=makeQuery(id+"F0.imprint","INTERSECT",VERTEX,{"derivedFrom":[subQ1,subQ0]});Q192=makeQuery(id+"F0.imprint","IMPRINT",FACE,{"disambiguationData":[TD([[makeQuery(id+"F0.imprint","IMPRINT",EDGE,{"disambiguationData":[TD([[subQ2,1.0]])],"derivedFrom":subQ1}),-1.0]])]});}
            var Q193;
            {var subQ0=sQuery(id+"F0.wireOp",EDGE,"E4.34.0");var subQ1=sQuery(id+"F0.wireOp",EDGE,"E1");var subQ2=makeQuery(id+"F0.imprint","INTERSECT",VERTEX,{"derivedFrom":[subQ1,subQ0]});Q193=makeQuery(id+"F0.imprint","IMPRINT",FACE,{"disambiguationData":[TD([[makeQuery(id+"F0.imprint","IMPRINT",EDGE,{"disambiguationData":[TD([[subQ2,1.0]])],"derivedFrom":subQ1}),-1.0]])]});}
            var Q194;
            {var subQ0=sQuery(id+"F0.wireOp",EDGE,"E4.33.0");var subQ1=sQuery(id+"F0.wireOp",EDGE,"E1");var subQ2=makeQuery(id+"F0.imprint","INTERSECT",VERTEX,{"derivedFrom":[subQ1,subQ0]});Q194=makeQuery(id+"F0.imprint","IMPRINT",FACE,{"disambiguationData":[TD([[makeQuery(id+"F0.imprint","IMPRINT",EDGE,{"disambiguationData":[TD([[subQ2,1.0]])],"derivedFrom":subQ1}),-1.0]])]});}
            var Q195;
            {var subQ0=sQuery(id+"F0.wireOp",EDGE,"E4.32.0");var subQ1=sQuery(id+"F0.wireOp",EDGE,"E1");var subQ2=makeQuery(id+"F0.imprint","INTERSECT",VERTEX,{"derivedFrom":[subQ1,subQ0]});Q195=makeQuery(id+"F0.imprint","IMPRINT",FACE,{"disambiguationData":[TD([[makeQuery(id+"F0.imprint","IMPRINT",EDGE,{"disambiguationData":[TD([[subQ2,1.0]])],"derivedFrom":subQ1}),-1.0]])]});}
            var Q196;
            {var subQ0=sQuery(id+"F0.wireOp",EDGE,"E4.31.0");var subQ1=sQuery(id+"F0.wireOp",EDGE,"E1");var subQ2=makeQuery(id+"F0.imprint","INTERSECT",VERTEX,{"derivedFrom":[subQ1,subQ0]});Q196=makeQuery(id+"F0.imprint","IMPRINT",FACE,{"disambiguationData":[TD([[makeQuery(id+"F0.imprint","IMPRINT",EDGE,{"disambiguationData":[TD([[subQ2,1.0]])],"derivedFrom":subQ1}),-1.0]])]});}
            var Q197;
            {var subQ0=sQuery(id+"F0.wireOp",EDGE,"E4.83.0");var subQ1=sQuery(id+"F0.wireOp",EDGE,"E1");var subQ2=makeQuery(id+"F0.imprint","INTERSECT",VERTEX,{"derivedFrom":[subQ1,subQ0]});Q197=makeQuery(id+"F0.imprint","IMPRINT",FACE,{"disambiguationData":[TD([[makeQuery(id+"F0.imprint","IMPRINT",EDGE,{"disambiguationData":[TD([[subQ2,1.0]])],"derivedFrom":subQ1}),-1.0]])]});}
            var Q198;
            {var subQ0=sQuery(id+"F0.wireOp",EDGE,"E4.51.0");var subQ1=sQuery(id+"F0.wireOp",EDGE,"E1");var subQ2=makeQuery(id+"F0.imprint","INTERSECT",VERTEX,{"derivedFrom":[subQ1,subQ0]});Q198=makeQuery(id+"F0.imprint","IMPRINT",FACE,{"disambiguationData":[TD([[makeQuery(id+"F0.imprint","IMPRINT",EDGE,{"disambiguationData":[TD([[subQ2,1.0]])],"derivedFrom":subQ1}),-1.0]])]});}
            var Q199;
            {var subQ0=sQuery(id+"F0.wireOp",EDGE,"E4.50.0");var subQ1=sQuery(id+"F0.wireOp",EDGE,"E1");var subQ2=makeQuery(id+"F0.imprint","INTERSECT",VERTEX,{"derivedFrom":[subQ1,subQ0]});Q199=makeQuery(id+"F0.imprint","IMPRINT",FACE,{"disambiguationData":[TD([[makeQuery(id+"F0.imprint","IMPRINT",EDGE,{"disambiguationData":[TD([[subQ2,1.0]])],"derivedFrom":subQ1}),-1.0]])]});}
            var Q200;
            {var subQ0=sQuery(id+"F0.wireOp",EDGE,"E4.49.0");var subQ1=sQuery(id+"F0.wireOp",EDGE,"E1");var subQ2=makeQuery(id+"F0.imprint","INTERSECT",VERTEX,{"derivedFrom":[subQ1,subQ0]});Q200=makeQuery(id+"F0.imprint","IMPRINT",FACE,{"disambiguationData":[TD([[makeQuery(id+"F0.imprint","IMPRINT",EDGE,{"disambiguationData":[TD([[subQ2,1.0]])],"derivedFrom":subQ1}),-1.0]])]});}
            var Q201;
            {var subQ0=sQuery(id+"F0.wireOp",EDGE,"E4.30.0");var subQ1=sQuery(id+"F0.wireOp",EDGE,"E1");var subQ2=makeQuery(id+"F0.imprint","INTERSECT",VERTEX,{"derivedFrom":[subQ1,subQ0]});Q201=makeQuery(id+"F0.imprint","IMPRINT",FACE,{"disambiguationData":[TD([[makeQuery(id+"F0.imprint","IMPRINT",EDGE,{"disambiguationData":[TD([[subQ2,1.0]])],"derivedFrom":subQ1}),-1.0]])]});}
            var Q202;
            {var subQ0=sQuery(id+"F0.wireOp",EDGE,"E4.72.0");var subQ1=sQuery(id+"F0.wireOp",EDGE,"E1");var subQ2=makeQuery(id+"F0.imprint","INTERSECT",VERTEX,{"derivedFrom":[subQ1,subQ0]});Q202=makeQuery(id+"F0.imprint","IMPRINT",FACE,{"disambiguationData":[TD([[makeQuery(id+"F0.imprint","IMPRINT",EDGE,{"disambiguationData":[TD([[subQ2,1.0]])],"derivedFrom":subQ1}),-1.0]])]});}
            var Q203;
            {var subQ0=sQuery(id+"F0.wireOp",EDGE,"E4.29.0");var subQ1=sQuery(id+"F0.wireOp",EDGE,"E1");var subQ2=makeQuery(id+"F0.imprint","INTERSECT",VERTEX,{"derivedFrom":[subQ1,subQ0]});Q203=makeQuery(id+"F0.imprint","IMPRINT",FACE,{"disambiguationData":[TD([[makeQuery(id+"F0.imprint","IMPRINT",EDGE,{"disambiguationData":[TD([[subQ2,1.0]])],"derivedFrom":subQ1}),-1.0]])]});}
            var Q204;
            {var subQ0=sQuery(id+"F0.wireOp",EDGE,"E4.47.0");var subQ1=sQuery(id+"F0.wireOp",EDGE,"E1");var subQ2=makeQuery(id+"F0.imprint","INTERSECT",VERTEX,{"derivedFrom":[subQ1,subQ0]});Q204=makeQuery(id+"F0.imprint","IMPRINT",FACE,{"disambiguationData":[TD([[makeQuery(id+"F0.imprint","IMPRINT",EDGE,{"disambiguationData":[TD([[subQ2,1.0]])],"derivedFrom":subQ1}),-1.0]])]});}
            var Q205;
            {var subQ0=sQuery(id+"F0.wireOp",EDGE,"E4.71.0");var subQ1=sQuery(id+"F0.wireOp",EDGE,"E1");var subQ2=makeQuery(id+"F0.imprint","INTERSECT",VERTEX,{"derivedFrom":[subQ1,subQ0]});Q205=makeQuery(id+"F0.imprint","IMPRINT",FACE,{"disambiguationData":[TD([[makeQuery(id+"F0.imprint","IMPRINT",EDGE,{"disambiguationData":[TD([[subQ2,1.0]])],"derivedFrom":subQ1}),-1.0]])]});}
            var Q206;
            {var subQ0=sQuery(id+"F0.wireOp",EDGE,"E4.43.0");var subQ1=sQuery(id+"F0.wireOp",EDGE,"E1");var subQ2=makeQuery(id+"F0.imprint","INTERSECT",VERTEX,{"derivedFrom":[subQ1,subQ0]});Q206=makeQuery(id+"F0.imprint","IMPRINT",FACE,{"disambiguationData":[TD([[makeQuery(id+"F0.imprint","IMPRINT",EDGE,{"disambiguationData":[TD([[subQ2,1.0]])],"derivedFrom":subQ1}),-1.0]])]});}
            var Q207;
            {var subQ0=sQuery(id+"F0.wireOp",EDGE,"E4.41.0");var subQ1=sQuery(id+"F0.wireOp",EDGE,"E1");var subQ2=makeQuery(id+"F0.imprint","INTERSECT",VERTEX,{"derivedFrom":[subQ1,subQ0]});Q207=makeQuery(id+"F0.imprint","IMPRINT",FACE,{"disambiguationData":[TD([[makeQuery(id+"F0.imprint","IMPRINT",EDGE,{"disambiguationData":[TD([[subQ2,1.0]])],"derivedFrom":subQ1}),-1.0]])]});}
            var Q208;
            {var subQ0=sQuery(id+"F0.wireOp",EDGE,"E4.48.0");var subQ1=sQuery(id+"F0.wireOp",EDGE,"E1");var subQ2=makeQuery(id+"F0.imprint","INTERSECT",VERTEX,{"derivedFrom":[subQ1,subQ0]});Q208=makeQuery(id+"F0.imprint","IMPRINT",FACE,{"disambiguationData":[TD([[makeQuery(id+"F0.imprint","IMPRINT",EDGE,{"disambiguationData":[TD([[subQ2,1.0]])],"derivedFrom":subQ1}),-1.0]])]});}
            var Q209;
            {var subQ0=sQuery(id+"F0.wireOp",EDGE,"E4.57.0");var subQ1=sQuery(id+"F0.wireOp",EDGE,"E1");var subQ2=makeQuery(id+"F0.imprint","INTERSECT",VERTEX,{"derivedFrom":[subQ1,subQ0]});Q209=makeQuery(id+"F0.imprint","IMPRINT",FACE,{"disambiguationData":[TD([[makeQuery(id+"F0.imprint","IMPRINT",EDGE,{"disambiguationData":[TD([[subQ2,1.0]])],"derivedFrom":subQ1}),-1.0]])]});}
            var Q210;
            {var subQ0=sQuery(id+"F0.wireOp",EDGE,"E4.56.0");var subQ1=sQuery(id+"F0.wireOp",EDGE,"E1");var subQ2=makeQuery(id+"F0.imprint","INTERSECT",VERTEX,{"derivedFrom":[subQ1,subQ0]});Q210=makeQuery(id+"F0.imprint","IMPRINT",FACE,{"disambiguationData":[TD([[makeQuery(id+"F0.imprint","IMPRINT",EDGE,{"disambiguationData":[TD([[subQ2,1.0]])],"derivedFrom":subQ1}),-1.0]])]});}
            var Q211;
            {var subQ0=sQuery(id+"F0.wireOp",EDGE,"E4.46.0");var subQ1=sQuery(id+"F0.wireOp",EDGE,"E1");var subQ2=makeQuery(id+"F0.imprint","INTERSECT",VERTEX,{"derivedFrom":[subQ1,subQ0]});Q211=makeQuery(id+"F0.imprint","IMPRINT",FACE,{"disambiguationData":[TD([[makeQuery(id+"F0.imprint","IMPRINT",EDGE,{"disambiguationData":[TD([[subQ2,1.0]])],"derivedFrom":subQ1}),-1.0]])]});}
            var Q212;
            {var subQ0=sQuery(id+"F0.wireOp",EDGE,"E4.44.0");var subQ1=sQuery(id+"F0.wireOp",EDGE,"E1");var subQ2=makeQuery(id+"F0.imprint","INTERSECT",VERTEX,{"derivedFrom":[subQ1,subQ0]});Q212=makeQuery(id+"F0.imprint","IMPRINT",FACE,{"disambiguationData":[TD([[makeQuery(id+"F0.imprint","IMPRINT",EDGE,{"disambiguationData":[TD([[subQ2,1.0]])],"derivedFrom":subQ1}),-1.0]])]});}
            var Q213;
            {var subQ0=sQuery(id+"F0.wireOp",EDGE,"E4.52.0");var subQ1=sQuery(id+"F0.wireOp",EDGE,"E1");var subQ2=makeQuery(id+"F0.imprint","INTERSECT",VERTEX,{"derivedFrom":[subQ1,subQ0]});Q213=makeQuery(id+"F0.imprint","IMPRINT",FACE,{"disambiguationData":[TD([[makeQuery(id+"F0.imprint","IMPRINT",EDGE,{"disambiguationData":[TD([[subQ2,1.0]])],"derivedFrom":subQ1}),-1.0]])]});}
            var Q214;
            {var subQ0=sQuery(id+"F0.wireOp",EDGE,"E4.45.0");var subQ1=sQuery(id+"F0.wireOp",EDGE,"E1");var subQ2=makeQuery(id+"F0.imprint","INTERSECT",VERTEX,{"derivedFrom":[subQ1,subQ0]});Q214=makeQuery(id+"F0.imprint","IMPRINT",FACE,{"disambiguationData":[TD([[makeQuery(id+"F0.imprint","IMPRINT",EDGE,{"disambiguationData":[TD([[subQ2,1.0]])],"derivedFrom":subQ1}),-1.0]])]});}
            var Q215;
            {var subQ0=sQuery(id+"F0.wireOp",EDGE,"E4.53.0");var subQ1=sQuery(id+"F0.wireOp",EDGE,"E1");var subQ2=makeQuery(id+"F0.imprint","INTERSECT",VERTEX,{"derivedFrom":[subQ1,subQ0]});Q215=makeQuery(id+"F0.imprint","IMPRINT",FACE,{"disambiguationData":[TD([[makeQuery(id+"F0.imprint","IMPRINT",EDGE,{"disambiguationData":[TD([[subQ2,1.0]])],"derivedFrom":subQ1}),-1.0]])]});}
            var Q216;
            {var subQ0=sQuery(id+"F0.wireOp",EDGE,"E4.54.0");var subQ1=sQuery(id+"F0.wireOp",EDGE,"E1");var subQ2=makeQuery(id+"F0.imprint","INTERSECT",VERTEX,{"derivedFrom":[subQ1,subQ0]});Q216=makeQuery(id+"F0.imprint","IMPRINT",FACE,{"disambiguationData":[TD([[makeQuery(id+"F0.imprint","IMPRINT",EDGE,{"disambiguationData":[TD([[subQ2,1.0]])],"derivedFrom":subQ1}),-1.0]])]});}
            var Q217;
            {var subQ0=sQuery(id+"F0.wireOp",EDGE,"E4.55.0");var subQ1=sQuery(id+"F0.wireOp",EDGE,"E1");var subQ2=makeQuery(id+"F0.imprint","INTERSECT",VERTEX,{"derivedFrom":[subQ1,subQ0]});Q217=makeQuery(id+"F0.imprint","IMPRINT",FACE,{"disambiguationData":[TD([[makeQuery(id+"F0.imprint","IMPRINT",EDGE,{"disambiguationData":[TD([[subQ2,1.0]])],"derivedFrom":subQ1}),-1.0]])]});}
            var Q218;
            {var subQ0=sQuery(id+"F0.wireOp",EDGE,"E4.58.0");var subQ1=sQuery(id+"F0.wireOp",EDGE,"E1");var subQ2=makeQuery(id+"F0.imprint","INTERSECT",VERTEX,{"derivedFrom":[subQ1,subQ0]});Q218=makeQuery(id+"F0.imprint","IMPRINT",FACE,{"disambiguationData":[TD([[makeQuery(id+"F0.imprint","IMPRINT",EDGE,{"disambiguationData":[TD([[subQ2,1.0]])],"derivedFrom":subQ1}),-1.0]])]});}
            var Q219;
            {var subQ0=sQuery(id+"F0.wireOp",EDGE,"E4.59.0");var subQ1=sQuery(id+"F0.wireOp",EDGE,"E1");var subQ2=makeQuery(id+"F0.imprint","INTERSECT",VERTEX,{"derivedFrom":[subQ1,subQ0]});Q219=makeQuery(id+"F0.imprint","IMPRINT",FACE,{"disambiguationData":[TD([[makeQuery(id+"F0.imprint","IMPRINT",EDGE,{"disambiguationData":[TD([[subQ2,1.0]])],"derivedFrom":subQ1}),-1.0]])]});}
            var Q220;
            {var subQ0=sQuery(id+"F0.wireOp",EDGE,"E4.60.0");var subQ1=sQuery(id+"F0.wireOp",EDGE,"E1");var subQ2=makeQuery(id+"F0.imprint","INTERSECT",VERTEX,{"derivedFrom":[subQ1,subQ0]});Q220=makeQuery(id+"F0.imprint","IMPRINT",FACE,{"disambiguationData":[TD([[makeQuery(id+"F0.imprint","IMPRINT",EDGE,{"disambiguationData":[TD([[subQ2,1.0]])],"derivedFrom":subQ1}),-1.0]])]});}
            extrude(context, id + "F1", {"entities" : qUnion([Q0, Q1, Q2, Q3, Q4, Q5, Q6, Q7, Q8, Q9, Q10, Q11, Q12, Q13, Q14, Q15, Q16, Q17, Q18, Q19, Q20, Q21, Q22, Q23, Q24, Q25, Q26, Q27, Q28, Q29, Q30, Q31, Q32, Q33, Q34, Q35, Q36, Q37, Q38, Q39, Q40, Q41, Q42, Q43, Q44, Q45, Q46, Q47, Q48, Q49, Q50, Q51, Q52, Q53, Q54, Q55, Q56, Q57, Q58, Q59, Q60, Q61, Q62, Q63, Q64, Q65, Q66, Q67, Q68, Q69, Q70, Q71, Q72, Q73, Q74, Q75, Q76, Q77, Q78, Q79, Q80, Q81, Q82, Q83, Q84, Q85, Q86, Q87, Q88, Q89, Q90, Q91, Q92, Q93, Q94, Q95, Q96, Q97, Q98, Q99, Q100, Q101, Q102, Q103, Q104, Q105, Q106, Q107, Q108, Q109, Q110, Q111, Q112, Q113, Q114, Q115, Q116, Q117, Q118, Q119, Q120, Q121, Q122, Q123, Q124, Q125, Q126, Q127, Q128, Q129, Q130, Q131, Q132, Q133, Q134, Q135, Q136, Q137, Q138, Q139, Q140, Q141, Q142, Q143, Q144, Q145, Q146, Q147, Q148, Q149, Q150, Q151, Q152, Q153, Q154, Q155, Q156, Q157, Q158, Q159, Q160, Q161, Q162, Q163, Q164, Q165, Q166, Q167, Q168, Q169, Q170, Q171, Q172, Q173, Q174, Q175, Q176, Q177, Q178, Q179, Q180, Q181, Q182, Q183, Q184, Q185, Q186, Q187, Q188, Q189, Q190, Q191, Q192, Q193, Q194, Q195, Q196, Q197, Q198, Q199, Q200, Q201, Q202, Q203, Q204, Q205, Q206, Q207, Q208, Q209, Q210, Q211, Q212, Q213, Q214, Q215, Q216, Q217, Q218, Q219, Q220]), "depth" : 5 * mm, "offsetDistance" : 25 * mm});
        }
    });
